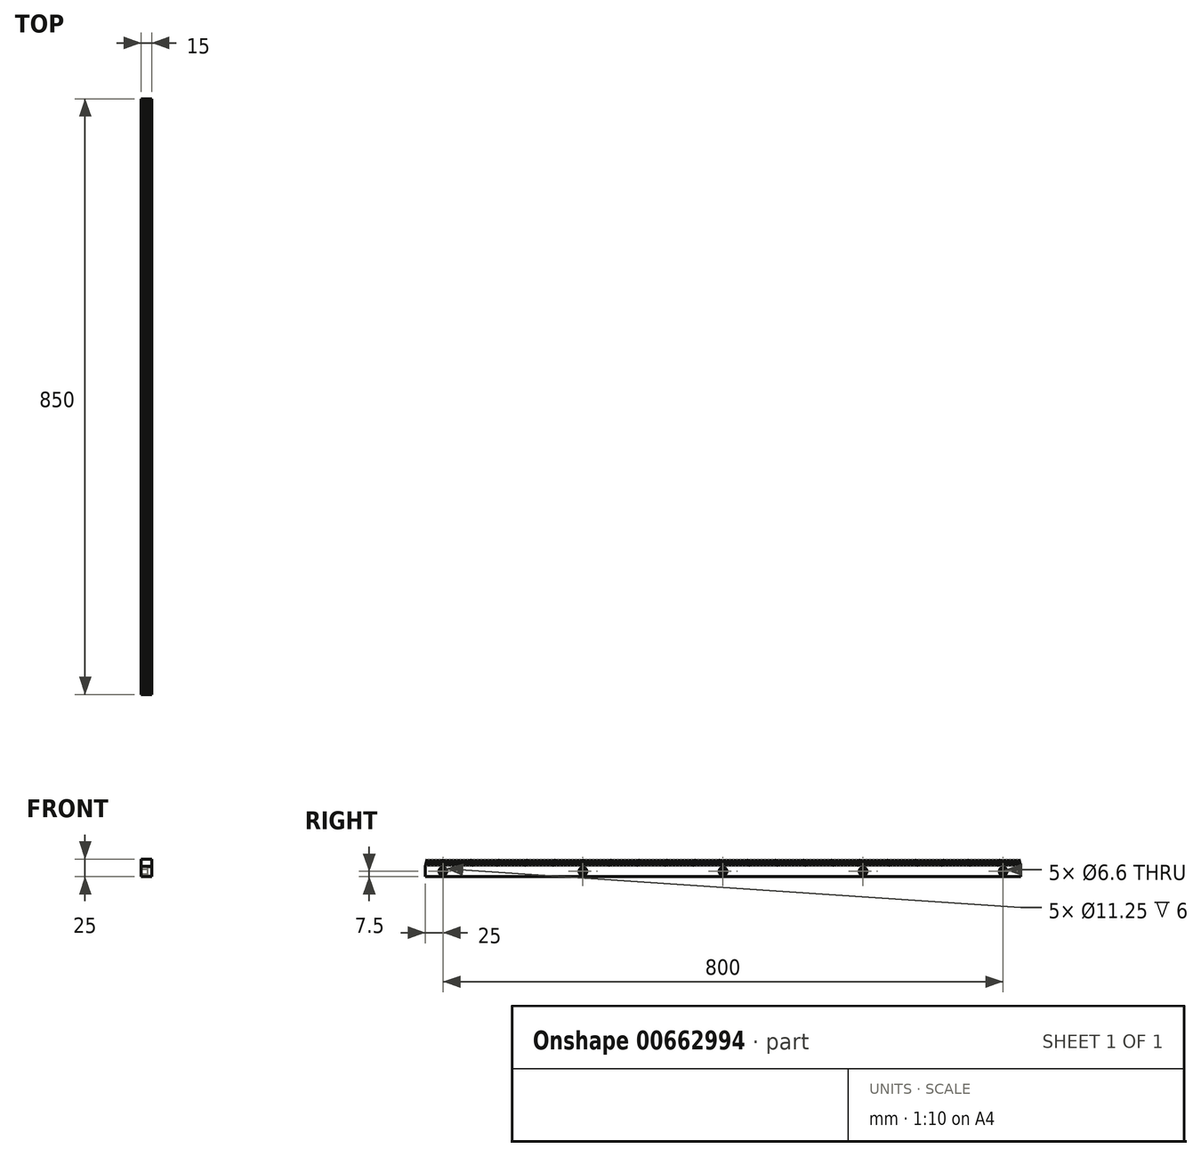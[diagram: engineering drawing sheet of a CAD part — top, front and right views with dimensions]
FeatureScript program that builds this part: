
annotation { "Feature Type Name" : "Feature", "Feature Type Description" : "" }
export const myFeature = defineFeature(function(context is Context, id is Id, definition is map)
    precondition{}
    {
        {
            var Q0;
            Q0=qCreatedBy(makeId("Right.planeOp"),FACE);
            var sketch = newSketch(context, id + "F0", { "sketchPlane" : qUnion([Q0])});
            skLineSegment(sketch, "E0", {"start": v(0, 0) * mm, "end": v(2.5, 10) * mm});
            skLineSegment(sketch, "E1", {"start": v(2.5, 10) * mm, "end": v(5, 0) * mm});
            skLineSegment(sketch, "E2.1.0.0", {"start": v(5, 0) * mm, "end": v(7.5, 10) * mm});
            skLineSegment(sketch, "E2.1.0.1", {"start": v(7.5, 10) * mm, "end": v(10, 0) * mm});
            skLineSegment(sketch, "E2.2.0.0", {"start": v(10, 0) * mm, "end": v(12.5, 10) * mm});
            skLineSegment(sketch, "E2.2.0.1", {"start": v(12.5, 10) * mm, "end": v(15, 0) * mm});
            skLineSegment(sketch, "E2.3.0.0", {"start": v(15, 0) * mm, "end": v(17.5, 10) * mm});
            skLineSegment(sketch, "E2.3.0.1", {"start": v(17.5, 10) * mm, "end": v(20, 0) * mm});
            skLineSegment(sketch, "E2.4.0.0", {"start": v(20, 0) * mm, "end": v(22.5, 10) * mm});
            skLineSegment(sketch, "E2.4.0.1", {"start": v(22.5, 10) * mm, "end": v(25, 0) * mm});
            skLineSegment(sketch, "E2.5.0.0", {"start": v(25, 0) * mm, "end": v(27.5, 10) * mm});
            skLineSegment(sketch, "E2.5.0.1", {"start": v(27.5, 10) * mm, "end": v(30, 0) * mm});
            skLineSegment(sketch, "E2.6.0.0", {"start": v(30, 0) * mm, "end": v(32.5, 10) * mm});
            skLineSegment(sketch, "E2.6.0.1", {"start": v(32.5, 10) * mm, "end": v(35, 0) * mm});
            skLineSegment(sketch, "E2.7.0.0", {"start": v(35, 0) * mm, "end": v(37.5, 10) * mm});
            skLineSegment(sketch, "E2.7.0.1", {"start": v(37.5, 10) * mm, "end": v(40, 0) * mm});
            skLineSegment(sketch, "E2.8.0.0", {"start": v(40, 0) * mm, "end": v(42.5, 10) * mm});
            skLineSegment(sketch, "E2.8.0.1", {"start": v(42.5, 10) * mm, "end": v(45, 0) * mm});
            skLineSegment(sketch, "E2.9.0.0", {"start": v(45, 0) * mm, "end": v(47.5, 10) * mm});
            skLineSegment(sketch, "E2.9.0.1", {"start": v(47.5, 10) * mm, "end": v(50, 0) * mm});
            skLineSegment(sketch, "E2.10.0.0", {"start": v(50, 0) * mm, "end": v(52.5, 10) * mm});
            skLineSegment(sketch, "E2.10.0.1", {"start": v(52.5, 10) * mm, "end": v(55, 0) * mm});
            skLineSegment(sketch, "E2.11.0.0", {"start": v(55, 0) * mm, "end": v(57.5, 10) * mm});
            skLineSegment(sketch, "E2.11.0.1", {"start": v(57.5, 10) * mm, "end": v(60, 0) * mm});
            skLineSegment(sketch, "E2.12.0.0", {"start": v(60, 0) * mm, "end": v(62.5, 10) * mm});
            skLineSegment(sketch, "E2.12.0.1", {"start": v(62.5, 10) * mm, "end": v(65, 0) * mm});
            skLineSegment(sketch, "E2.13.0.0", {"start": v(65, 0) * mm, "end": v(67.5, 10) * mm});
            skLineSegment(sketch, "E2.13.0.1", {"start": v(67.5, 10) * mm, "end": v(70, 0) * mm});
            skLineSegment(sketch, "E2.14.0.0", {"start": v(70, 0) * mm, "end": v(72.5, 10) * mm});
            skLineSegment(sketch, "E2.14.0.1", {"start": v(72.5, 10) * mm, "end": v(75, 0) * mm});
            skLineSegment(sketch, "E2.15.0.0", {"start": v(75, 0) * mm, "end": v(77.5, 10) * mm});
            skLineSegment(sketch, "E2.15.0.1", {"start": v(77.5, 10) * mm, "end": v(80, 0) * mm});
            skLineSegment(sketch, "E2.16.0.0", {"start": v(80, 0) * mm, "end": v(82.5, 10) * mm});
            skLineSegment(sketch, "E2.16.0.1", {"start": v(82.5, 10) * mm, "end": v(85, 0) * mm});
            skLineSegment(sketch, "E2.17.0.0", {"start": v(85, 0) * mm, "end": v(87.5, 10) * mm});
            skLineSegment(sketch, "E2.17.0.1", {"start": v(87.5, 10) * mm, "end": v(90, 0) * mm});
            skLineSegment(sketch, "E2.18.0.0", {"start": v(90, 0) * mm, "end": v(92.5, 10) * mm});
            skLineSegment(sketch, "E2.18.0.1", {"start": v(92.5, 10) * mm, "end": v(95, 0) * mm});
            skLineSegment(sketch, "E2.19.0.0", {"start": v(95, 0) * mm, "end": v(97.5, 10) * mm});
            skLineSegment(sketch, "E2.19.0.1", {"start": v(97.5, 10) * mm, "end": v(100, 0) * mm});
            skLineSegment(sketch, "E2.20.0.0", {"start": v(100, 0) * mm, "end": v(102.5, 10) * mm});
            skLineSegment(sketch, "E2.20.0.1", {"start": v(102.5, 10) * mm, "end": v(105, 0) * mm});
            skLineSegment(sketch, "E2.21.0.0", {"start": v(105, 0) * mm, "end": v(107.5, 10) * mm});
            skLineSegment(sketch, "E2.21.0.1", {"start": v(107.5, 10) * mm, "end": v(110, 0) * mm});
            skLineSegment(sketch, "E2.22.0.0", {"start": v(110, 0) * mm, "end": v(112.5, 10) * mm});
            skLineSegment(sketch, "E2.22.0.1", {"start": v(112.5, 10) * mm, "end": v(115, 0) * mm});
            skLineSegment(sketch, "E2.23.0.0", {"start": v(115, 0) * mm, "end": v(117.5, 10) * mm});
            skLineSegment(sketch, "E2.23.0.1", {"start": v(117.5, 10) * mm, "end": v(120, 0) * mm});
            skLineSegment(sketch, "E2.24.0.0", {"start": v(120, 0) * mm, "end": v(122.5, 10) * mm});
            skLineSegment(sketch, "E2.24.0.1", {"start": v(122.5, 10) * mm, "end": v(125, 0) * mm});
            skLineSegment(sketch, "E2.25.0.0", {"start": v(125, 0) * mm, "end": v(127.5, 10) * mm});
            skLineSegment(sketch, "E2.25.0.1", {"start": v(127.5, 10) * mm, "end": v(130, 0) * mm});
            skLineSegment(sketch, "E2.26.0.0", {"start": v(130, 0) * mm, "end": v(132.5, 10) * mm});
            skLineSegment(sketch, "E2.26.0.1", {"start": v(132.5, 10) * mm, "end": v(135, 0) * mm});
            skLineSegment(sketch, "E2.27.0.0", {"start": v(135, 0) * mm, "end": v(137.5, 10) * mm});
            skLineSegment(sketch, "E2.27.0.1", {"start": v(137.5, 10) * mm, "end": v(140, 0) * mm});
            skLineSegment(sketch, "E2.28.0.0", {"start": v(140, 0) * mm, "end": v(142.5, 10) * mm});
            skLineSegment(sketch, "E2.28.0.1", {"start": v(142.5, 10) * mm, "end": v(145, 0) * mm});
            skLineSegment(sketch, "E2.29.0.0", {"start": v(145, 0) * mm, "end": v(147.5, 10) * mm});
            skLineSegment(sketch, "E2.29.0.1", {"start": v(147.5, 10) * mm, "end": v(150, 0) * mm});
            skLineSegment(sketch, "E2.30.0.0", {"start": v(150, 0) * mm, "end": v(152.5, 10) * mm});
            skLineSegment(sketch, "E2.30.0.1", {"start": v(152.5, 10) * mm, "end": v(155, 0) * mm});
            skLineSegment(sketch, "E2.31.0.0", {"start": v(155, 0) * mm, "end": v(157.5, 10) * mm});
            skLineSegment(sketch, "E2.31.0.1", {"start": v(157.5, 10) * mm, "end": v(160, 0) * mm});
            skLineSegment(sketch, "E2.32.0.0", {"start": v(160, 0) * mm, "end": v(162.5, 10) * mm});
            skLineSegment(sketch, "E2.32.0.1", {"start": v(162.5, 10) * mm, "end": v(165, 0) * mm});
            skLineSegment(sketch, "E2.33.0.0", {"start": v(165, 0) * mm, "end": v(167.5, 10) * mm});
            skLineSegment(sketch, "E2.33.0.1", {"start": v(167.5, 10) * mm, "end": v(170, 0) * mm});
            skLineSegment(sketch, "E2.34.0.0", {"start": v(170, 0) * mm, "end": v(172.5, 10) * mm});
            skLineSegment(sketch, "E2.34.0.1", {"start": v(172.5, 10) * mm, "end": v(175, 0) * mm});
            skLineSegment(sketch, "E2.35.0.0", {"start": v(175, 0) * mm, "end": v(177.5, 10) * mm});
            skLineSegment(sketch, "E2.35.0.1", {"start": v(177.5, 10) * mm, "end": v(180, 0) * mm});
            skLineSegment(sketch, "E2.36.0.0", {"start": v(180, 0) * mm, "end": v(182.5, 10) * mm});
            skLineSegment(sketch, "E2.36.0.1", {"start": v(182.5, 10) * mm, "end": v(185, 0) * mm});
            skLineSegment(sketch, "E2.37.0.0", {"start": v(185, 0) * mm, "end": v(187.5, 10) * mm});
            skLineSegment(sketch, "E2.37.0.1", {"start": v(187.5, 10) * mm, "end": v(190, 0) * mm});
            skLineSegment(sketch, "E2.38.0.0", {"start": v(190, 0) * mm, "end": v(192.5, 10) * mm});
            skLineSegment(sketch, "E2.38.0.1", {"start": v(192.5, 10) * mm, "end": v(195, 0) * mm});
            skLineSegment(sketch, "E2.39.0.0", {"start": v(195, 0) * mm, "end": v(197.5, 10) * mm});
            skLineSegment(sketch, "E2.39.0.1", {"start": v(197.5, 10) * mm, "end": v(200, 0) * mm});
            skLineSegment(sketch, "E2.40.0.0", {"start": v(200, 0) * mm, "end": v(202.5, 10) * mm});
            skLineSegment(sketch, "E2.40.0.1", {"start": v(202.5, 10) * mm, "end": v(205, 0) * mm});
            skLineSegment(sketch, "E2.41.0.0", {"start": v(205, 0) * mm, "end": v(207.5, 10) * mm});
            skLineSegment(sketch, "E2.41.0.1", {"start": v(207.5, 10) * mm, "end": v(210, 0) * mm});
            skLineSegment(sketch, "E2.42.0.0", {"start": v(210, 0) * mm, "end": v(212.5, 10) * mm});
            skLineSegment(sketch, "E2.42.0.1", {"start": v(212.5, 10) * mm, "end": v(215, 0) * mm});
            skLineSegment(sketch, "E2.43.0.0", {"start": v(215, 0) * mm, "end": v(217.5, 10) * mm});
            skLineSegment(sketch, "E2.43.0.1", {"start": v(217.5, 10) * mm, "end": v(220, 0) * mm});
            skLineSegment(sketch, "E2.44.0.0", {"start": v(220, 0) * mm, "end": v(222.5, 10) * mm});
            skLineSegment(sketch, "E2.44.0.1", {"start": v(222.5, 10) * mm, "end": v(225, 0) * mm});
            skLineSegment(sketch, "E2.45.0.0", {"start": v(225, 0) * mm, "end": v(227.5, 10) * mm});
            skLineSegment(sketch, "E2.45.0.1", {"start": v(227.5, 10) * mm, "end": v(230, 0) * mm});
            skLineSegment(sketch, "E2.46.0.0", {"start": v(230, 0) * mm, "end": v(232.5, 10) * mm});
            skLineSegment(sketch, "E2.46.0.1", {"start": v(232.5, 10) * mm, "end": v(235, 0) * mm});
            skLineSegment(sketch, "E2.47.0.0", {"start": v(235, 0) * mm, "end": v(237.5, 10) * mm});
            skLineSegment(sketch, "E2.47.0.1", {"start": v(237.5, 10) * mm, "end": v(240, 0) * mm});
            skLineSegment(sketch, "E2.48.0.0", {"start": v(240, 0) * mm, "end": v(242.5, 10) * mm});
            skLineSegment(sketch, "E2.48.0.1", {"start": v(242.5, 10) * mm, "end": v(245, 0) * mm});
            skLineSegment(sketch, "E2.49.0.0", {"start": v(245, 0) * mm, "end": v(247.5, 10) * mm});
            skLineSegment(sketch, "E2.49.0.1", {"start": v(247.5, 10) * mm, "end": v(250, 0) * mm});
            skLineSegment(sketch, "E2.50.0.0", {"start": v(250, 0) * mm, "end": v(252.5, 10) * mm});
            skLineSegment(sketch, "E2.50.0.1", {"start": v(252.5, 10) * mm, "end": v(255, 0) * mm});
            skLineSegment(sketch, "E2.51.0.0", {"start": v(255, 0) * mm, "end": v(257.5, 10) * mm});
            skLineSegment(sketch, "E2.51.0.1", {"start": v(257.5, 10) * mm, "end": v(260, 0) * mm});
            skLineSegment(sketch, "E2.52.0.0", {"start": v(260, 0) * mm, "end": v(262.5, 10) * mm});
            skLineSegment(sketch, "E2.52.0.1", {"start": v(262.5, 10) * mm, "end": v(265, 0) * mm});
            skLineSegment(sketch, "E2.53.0.0", {"start": v(265, 0) * mm, "end": v(267.5, 10) * mm});
            skLineSegment(sketch, "E2.53.0.1", {"start": v(267.5, 10) * mm, "end": v(270, 0) * mm});
            skLineSegment(sketch, "E2.54.0.0", {"start": v(270, 0) * mm, "end": v(272.5, 10) * mm});
            skLineSegment(sketch, "E2.54.0.1", {"start": v(272.5, 10) * mm, "end": v(275, 0) * mm});
            skLineSegment(sketch, "E2.55.0.0", {"start": v(275, 0) * mm, "end": v(277.5, 10) * mm});
            skLineSegment(sketch, "E2.55.0.1", {"start": v(277.5, 10) * mm, "end": v(280, 0) * mm});
            skLineSegment(sketch, "E2.56.0.0", {"start": v(280, 0) * mm, "end": v(282.5, 10) * mm});
            skLineSegment(sketch, "E2.56.0.1", {"start": v(282.5, 10) * mm, "end": v(285, 0) * mm});
            skLineSegment(sketch, "E2.57.0.0", {"start": v(285, 0) * mm, "end": v(287.5, 10) * mm});
            skLineSegment(sketch, "E2.57.0.1", {"start": v(287.5, 10) * mm, "end": v(290, 0) * mm});
            skLineSegment(sketch, "E2.58.0.0", {"start": v(290, 0) * mm, "end": v(292.5, 10) * mm});
            skLineSegment(sketch, "E2.58.0.1", {"start": v(292.5, 10) * mm, "end": v(295, 0) * mm});
            skLineSegment(sketch, "E2.59.0.0", {"start": v(295, 0) * mm, "end": v(297.5, 10) * mm});
            skLineSegment(sketch, "E2.59.0.1", {"start": v(297.5, 10) * mm, "end": v(300, 0) * mm});
            skLineSegment(sketch, "E2.60.0.0", {"start": v(300, 0) * mm, "end": v(302.5, 10) * mm});
            skLineSegment(sketch, "E2.60.0.1", {"start": v(302.5, 10) * mm, "end": v(305, 0) * mm});
            skLineSegment(sketch, "E2.61.0.0", {"start": v(305, 0) * mm, "end": v(307.5, 10) * mm});
            skLineSegment(sketch, "E2.61.0.1", {"start": v(307.5, 10) * mm, "end": v(310, 0) * mm});
            skLineSegment(sketch, "E2.62.0.0", {"start": v(310, 0) * mm, "end": v(312.5, 10) * mm});
            skLineSegment(sketch, "E2.62.0.1", {"start": v(312.5, 10) * mm, "end": v(315, 0) * mm});
            skLineSegment(sketch, "E2.63.0.0", {"start": v(315, 0) * mm, "end": v(317.5, 10) * mm});
            skLineSegment(sketch, "E2.63.0.1", {"start": v(317.5, 10) * mm, "end": v(320, 0) * mm});
            skLineSegment(sketch, "E2.64.0.0", {"start": v(320, 0) * mm, "end": v(322.5, 10) * mm});
            skLineSegment(sketch, "E2.64.0.1", {"start": v(322.5, 10) * mm, "end": v(325, 0) * mm});
            skLineSegment(sketch, "E2.65.0.0", {"start": v(325, 0) * mm, "end": v(327.5, 10) * mm});
            skLineSegment(sketch, "E2.65.0.1", {"start": v(327.5, 10) * mm, "end": v(330, 0) * mm});
            skLineSegment(sketch, "E2.66.0.0", {"start": v(330, 0) * mm, "end": v(332.5, 10) * mm});
            skLineSegment(sketch, "E2.66.0.1", {"start": v(332.5, 10) * mm, "end": v(335, 0) * mm});
            skLineSegment(sketch, "E2.67.0.0", {"start": v(335, 0) * mm, "end": v(337.5, 10) * mm});
            skLineSegment(sketch, "E2.67.0.1", {"start": v(337.5, 10) * mm, "end": v(340, 0) * mm});
            skLineSegment(sketch, "E2.68.0.0", {"start": v(340, 0) * mm, "end": v(342.5, 10) * mm});
            skLineSegment(sketch, "E2.68.0.1", {"start": v(342.5, 10) * mm, "end": v(345, 0) * mm});
            skLineSegment(sketch, "E2.69.0.0", {"start": v(345, 0) * mm, "end": v(347.5, 10) * mm});
            skLineSegment(sketch, "E2.69.0.1", {"start": v(347.5, 10) * mm, "end": v(350, 0) * mm});
            skLineSegment(sketch, "E2.70.0.0", {"start": v(350, 0) * mm, "end": v(352.5, 10) * mm});
            skLineSegment(sketch, "E2.70.0.1", {"start": v(352.5, 10) * mm, "end": v(355, 0) * mm});
            skLineSegment(sketch, "E2.71.0.0", {"start": v(355, 0) * mm, "end": v(357.5, 10) * mm});
            skLineSegment(sketch, "E2.71.0.1", {"start": v(357.5, 10) * mm, "end": v(360, 0) * mm});
            skLineSegment(sketch, "E2.72.0.0", {"start": v(360, 0) * mm, "end": v(362.5, 10) * mm});
            skLineSegment(sketch, "E2.72.0.1", {"start": v(362.5, 10) * mm, "end": v(365, 0) * mm});
            skLineSegment(sketch, "E2.73.0.0", {"start": v(365, 0) * mm, "end": v(367.5, 10) * mm});
            skLineSegment(sketch, "E2.73.0.1", {"start": v(367.5, 10) * mm, "end": v(370, 0) * mm});
            skLineSegment(sketch, "E2.74.0.0", {"start": v(370, 0) * mm, "end": v(372.5, 10) * mm});
            skLineSegment(sketch, "E2.74.0.1", {"start": v(372.5, 10) * mm, "end": v(375, 0) * mm});
            skLineSegment(sketch, "E2.75.0.0", {"start": v(375, 0) * mm, "end": v(377.5, 10) * mm});
            skLineSegment(sketch, "E2.75.0.1", {"start": v(377.5, 10) * mm, "end": v(380, 0) * mm});
            skLineSegment(sketch, "E2.76.0.0", {"start": v(380, 0) * mm, "end": v(382.5, 10) * mm});
            skLineSegment(sketch, "E2.76.0.1", {"start": v(382.5, 10) * mm, "end": v(385, 0) * mm});
            skLineSegment(sketch, "E2.77.0.0", {"start": v(385, 0) * mm, "end": v(387.5, 10) * mm});
            skLineSegment(sketch, "E2.77.0.1", {"start": v(387.5, 10) * mm, "end": v(390, 0) * mm});
            skLineSegment(sketch, "E2.78.0.0", {"start": v(390, 0) * mm, "end": v(392.5, 10) * mm});
            skLineSegment(sketch, "E2.78.0.1", {"start": v(392.5, 10) * mm, "end": v(395, 0) * mm});
            skLineSegment(sketch, "E2.79.0.0", {"start": v(395, 0) * mm, "end": v(397.5, 10) * mm});
            skLineSegment(sketch, "E2.79.0.1", {"start": v(397.5, 10) * mm, "end": v(400, 0) * mm});
            skLineSegment(sketch, "E2.80.0.0", {"start": v(400, 0) * mm, "end": v(402.5, 10) * mm});
            skLineSegment(sketch, "E2.80.0.1", {"start": v(402.5, 10) * mm, "end": v(405, 0) * mm});
            skLineSegment(sketch, "E2.81.0.0", {"start": v(405, 0) * mm, "end": v(407.5, 10) * mm});
            skLineSegment(sketch, "E2.81.0.1", {"start": v(407.5, 10) * mm, "end": v(410, 0) * mm});
            skLineSegment(sketch, "E2.82.0.0", {"start": v(410, 0) * mm, "end": v(412.5, 10) * mm});
            skLineSegment(sketch, "E2.82.0.1", {"start": v(412.5, 10) * mm, "end": v(415, 0) * mm});
            skLineSegment(sketch, "E2.83.0.0", {"start": v(415, 0) * mm, "end": v(417.5, 10) * mm});
            skLineSegment(sketch, "E2.83.0.1", {"start": v(417.5, 10) * mm, "end": v(420, 0) * mm});
            skLineSegment(sketch, "E2.84.0.0", {"start": v(420, 0) * mm, "end": v(422.5, 10) * mm});
            skLineSegment(sketch, "E2.84.0.1", {"start": v(422.5, 10) * mm, "end": v(425, 0) * mm});
            skLineSegment(sketch, "E2.direction1", {"start": v(0, 0) * mm, "end": v(5, 0) * mm, "construction": true});
            skLineSegment(sketch, "E3.1.0.0", {"start": v(847.5, 10) * mm, "end": v(850, 0) * mm});
            skLineSegment(sketch, "E3.1.0.1", {"start": v(427.5, 10) * mm, "end": v(430, 0) * mm});
            skLineSegment(sketch, "E3.1.0.2", {"start": v(432.5, 10) * mm, "end": v(435, 0) * mm});
            skLineSegment(sketch, "E3.1.0.3", {"start": v(437.5, 10) * mm, "end": v(440, 0) * mm});
            skLineSegment(sketch, "E3.1.0.4", {"start": v(845, 0) * mm, "end": v(847.5, 10) * mm});
            skLineSegment(sketch, "E3.1.0.5", {"start": v(442.5, 10) * mm, "end": v(445, 0) * mm});
            skLineSegment(sketch, "E3.1.0.6", {"start": v(447.5, 10) * mm, "end": v(450, 0) * mm});
            skLineSegment(sketch, "E3.1.0.7", {"start": v(450, 0) * mm, "end": v(452.5, 10) * mm});
            skLineSegment(sketch, "E3.1.0.8", {"start": v(587.5, 10) * mm, "end": v(590, 0) * mm});
            skLineSegment(sketch, "E3.1.0.9", {"start": v(590, 0) * mm, "end": v(592.5, 10) * mm});
            skLineSegment(sketch, "E3.1.0.10", {"start": v(585, 0) * mm, "end": v(587.5, 10) * mm});
            skLineSegment(sketch, "E3.1.0.11", {"start": v(842.5, 10) * mm, "end": v(845, 0) * mm});
            skLineSegment(sketch, "E3.1.0.12", {"start": v(462.5, 10) * mm, "end": v(465, 0) * mm});
            skLineSegment(sketch, "E3.1.0.13", {"start": v(460, 0) * mm, "end": v(462.5, 10) * mm});
            skLineSegment(sketch, "E3.1.0.14", {"start": v(425, 0) * mm, "end": v(427.5, 10) * mm});
            skLineSegment(sketch, "E3.1.0.15", {"start": v(430, 0) * mm, "end": v(432.5, 10) * mm});
            skLineSegment(sketch, "E3.1.0.16", {"start": v(435, 0) * mm, "end": v(437.5, 10) * mm});
            skLineSegment(sketch, "E3.1.0.17", {"start": v(557.5, 10) * mm, "end": v(560, 0) * mm});
            skLineSegment(sketch, "E3.1.0.18", {"start": v(517.5, 10) * mm, "end": v(520, 0) * mm});
            skLineSegment(sketch, "E3.1.0.19", {"start": v(477.5, 10) * mm, "end": v(480, 0) * mm});
            skLineSegment(sketch, "E3.1.0.20", {"start": v(440, 0) * mm, "end": v(442.5, 10) * mm});
            skLineSegment(sketch, "E3.1.0.21", {"start": v(677.5, 10) * mm, "end": v(680, 0) * mm});
            skLineSegment(sketch, "E3.1.0.22", {"start": v(637.5, 10) * mm, "end": v(640, 0) * mm});
            skLineSegment(sketch, "E3.1.0.23", {"start": v(597.5, 10) * mm, "end": v(600, 0) * mm});
            skLineSegment(sketch, "E3.1.0.24", {"start": v(542.5, 10) * mm, "end": v(545, 0) * mm});
            skLineSegment(sketch, "E3.1.0.25", {"start": v(552.5, 10) * mm, "end": v(555, 0) * mm});
            skLineSegment(sketch, "E3.1.0.26", {"start": v(512.5, 10) * mm, "end": v(515, 0) * mm});
            skLineSegment(sketch, "E3.1.0.27", {"start": v(502.5, 10) * mm, "end": v(505, 0) * mm});
            skLineSegment(sketch, "E3.1.0.28", {"start": v(837.5, 10) * mm, "end": v(840, 0) * mm});
            skLineSegment(sketch, "E3.1.0.29", {"start": v(472.5, 10) * mm, "end": v(475, 0) * mm});
            skLineSegment(sketch, "E3.1.0.30", {"start": v(797.5, 10) * mm, "end": v(800, 0) * mm});
            skLineSegment(sketch, "E3.1.0.31", {"start": v(445, 0) * mm, "end": v(447.5, 10) * mm});
            skLineSegment(sketch, "E3.1.0.32", {"start": v(702.5, 10) * mm, "end": v(705, 0) * mm});
            skLineSegment(sketch, "E3.1.0.33", {"start": v(712.5, 10) * mm, "end": v(715, 0) * mm});
            skLineSegment(sketch, "E3.1.0.34", {"start": v(662.5, 10) * mm, "end": v(665, 0) * mm});
            skLineSegment(sketch, "E3.1.0.35", {"start": v(672.5, 10) * mm, "end": v(675, 0) * mm});
            skLineSegment(sketch, "E3.1.0.36", {"start": v(622.5, 10) * mm, "end": v(625, 0) * mm});
            skLineSegment(sketch, "E3.1.0.37", {"start": v(632.5, 10) * mm, "end": v(635, 0) * mm});
            skLineSegment(sketch, "E3.1.0.38", {"start": v(592.5, 10) * mm, "end": v(595, 0) * mm});
            skLineSegment(sketch, "E3.1.0.39", {"start": v(582.5, 10) * mm, "end": v(585, 0) * mm});
            skLineSegment(sketch, "E3.1.0.40", {"start": v(547.5, 10) * mm, "end": v(550, 0) * mm});
            skLineSegment(sketch, "E3.1.0.41", {"start": v(507.5, 10) * mm, "end": v(510, 0) * mm});
            skLineSegment(sketch, "E3.1.0.42", {"start": v(832.5, 10) * mm, "end": v(835, 0) * mm});
            skLineSegment(sketch, "E3.1.0.43", {"start": v(467.5, 10) * mm, "end": v(470, 0) * mm});
            skLineSegment(sketch, "E3.1.0.44", {"start": v(792.5, 10) * mm, "end": v(795, 0) * mm});
            skLineSegment(sketch, "E3.1.0.45", {"start": v(752.5, 10) * mm, "end": v(755, 0) * mm});
            skLineSegment(sketch, "E3.1.0.46", {"start": v(707.5, 10) * mm, "end": v(710, 0) * mm});
            skLineSegment(sketch, "E3.1.0.47", {"start": v(667.5, 10) * mm, "end": v(670, 0) * mm});
            skLineSegment(sketch, "E3.1.0.48", {"start": v(627.5, 10) * mm, "end": v(630, 0) * mm});
            skLineSegment(sketch, "E3.1.0.49", {"start": v(452.5, 10) * mm, "end": v(455, 0) * mm});
            skLineSegment(sketch, "E3.1.0.50", {"start": v(455, 0) * mm, "end": v(457.5, 10) * mm});
            skLineSegment(sketch, "E3.1.0.51", {"start": v(800, 0) * mm, "end": v(802.5, 10) * mm});
            skLineSegment(sketch, "E3.1.0.52", {"start": v(760, 0) * mm, "end": v(762.5, 10) * mm});
            skLineSegment(sketch, "E3.1.0.53", {"start": v(720, 0) * mm, "end": v(722.5, 10) * mm});
            skLineSegment(sketch, "E3.1.0.54", {"start": v(680, 0) * mm, "end": v(682.5, 10) * mm});
            skLineSegment(sketch, "E3.1.0.55", {"start": v(840, 0) * mm, "end": v(842.5, 10) * mm});
            skLineSegment(sketch, "E3.1.0.56", {"start": v(802.5, 10) * mm, "end": v(805, 0) * mm});
            skLineSegment(sketch, "E3.1.0.57", {"start": v(722.5, 10) * mm, "end": v(725, 0) * mm});
            skLineSegment(sketch, "E3.1.0.58", {"start": v(682.5, 10) * mm, "end": v(685, 0) * mm});
            skLineSegment(sketch, "E3.1.0.59", {"start": v(555, 0) * mm, "end": v(557.5, 10) * mm});
            skLineSegment(sketch, "E3.1.0.60", {"start": v(515, 0) * mm, "end": v(517.5, 10) * mm});
            skLineSegment(sketch, "E3.1.0.61", {"start": v(475, 0) * mm, "end": v(477.5, 10) * mm});
            skLineSegment(sketch, "E3.1.0.62", {"start": v(715, 0) * mm, "end": v(717.5, 10) * mm});
            skLineSegment(sketch, "E3.1.0.63", {"start": v(675, 0) * mm, "end": v(677.5, 10) * mm});
            skLineSegment(sketch, "E3.1.0.64", {"start": v(635, 0) * mm, "end": v(637.5, 10) * mm});
            skLineSegment(sketch, "E3.1.0.65", {"start": v(595, 0) * mm, "end": v(597.5, 10) * mm});
            skLineSegment(sketch, "E3.1.0.66", {"start": v(550, 0) * mm, "end": v(552.5, 10) * mm});
            skLineSegment(sketch, "E3.1.0.67", {"start": v(510, 0) * mm, "end": v(512.5, 10) * mm});
            skLineSegment(sketch, "E3.1.0.68", {"start": v(835, 0) * mm, "end": v(837.5, 10) * mm});
            skLineSegment(sketch, "E3.1.0.69", {"start": v(470, 0) * mm, "end": v(472.5, 10) * mm});
            skLineSegment(sketch, "E3.1.0.70", {"start": v(795, 0) * mm, "end": v(797.5, 10) * mm});
            skLineSegment(sketch, "E3.1.0.71", {"start": v(755, 0) * mm, "end": v(757.5, 10) * mm});
            skLineSegment(sketch, "E3.1.0.72", {"start": v(710, 0) * mm, "end": v(712.5, 10) * mm});
            skLineSegment(sketch, "E3.1.0.73", {"start": v(670, 0) * mm, "end": v(672.5, 10) * mm});
            skLineSegment(sketch, "E3.1.0.74", {"start": v(630, 0) * mm, "end": v(632.5, 10) * mm});
            skLineSegment(sketch, "E3.1.0.75", {"start": v(545, 0) * mm, "end": v(547.5, 10) * mm});
            skLineSegment(sketch, "E3.1.0.76", {"start": v(505, 0) * mm, "end": v(507.5, 10) * mm});
            skLineSegment(sketch, "E3.1.0.77", {"start": v(830, 0) * mm, "end": v(832.5, 10) * mm});
            skLineSegment(sketch, "E3.1.0.78", {"start": v(465, 0) * mm, "end": v(467.5, 10) * mm});
            skLineSegment(sketch, "E3.1.0.79", {"start": v(790, 0) * mm, "end": v(792.5, 10) * mm});
            skLineSegment(sketch, "E3.1.0.80", {"start": v(750, 0) * mm, "end": v(752.5, 10) * mm});
            skLineSegment(sketch, "E3.1.0.81", {"start": v(705, 0) * mm, "end": v(707.5, 10) * mm});
            skLineSegment(sketch, "E3.1.0.82", {"start": v(665, 0) * mm, "end": v(667.5, 10) * mm});
            skLineSegment(sketch, "E3.1.0.83", {"start": v(625, 0) * mm, "end": v(627.5, 10) * mm});
            skLineSegment(sketch, "E3.1.0.84", {"start": v(457.5, 10) * mm, "end": v(460, 0) * mm});
            skLineSegment(sketch, "E3.1.0.85", {"start": v(495, 0) * mm, "end": v(497.5, 10) * mm});
            skLineSegment(sketch, "E3.1.0.86", {"start": v(655, 0) * mm, "end": v(657.5, 10) * mm});
            skLineSegment(sketch, "E3.1.0.87", {"start": v(615, 0) * mm, "end": v(617.5, 10) * mm});
            skLineSegment(sketch, "E3.1.0.88", {"start": v(575, 0) * mm, "end": v(577.5, 10) * mm});
            skLineSegment(sketch, "E3.1.0.89", {"start": v(535, 0) * mm, "end": v(537.5, 10) * mm});
            skLineSegment(sketch, "E3.1.0.90", {"start": v(490, 0) * mm, "end": v(492.5, 10) * mm});
            skLineSegment(sketch, "E3.1.0.91", {"start": v(815, 0) * mm, "end": v(817.5, 10) * mm});
            skLineSegment(sketch, "E3.1.0.92", {"start": v(775, 0) * mm, "end": v(777.5, 10) * mm});
            skLineSegment(sketch, "E3.1.0.93", {"start": v(735, 0) * mm, "end": v(737.5, 10) * mm});
            skLineSegment(sketch, "E3.1.0.94", {"start": v(695, 0) * mm, "end": v(697.5, 10) * mm});
            skLineSegment(sketch, "E3.1.0.95", {"start": v(650, 0) * mm, "end": v(652.5, 10) * mm});
            skLineSegment(sketch, "E3.1.0.96", {"start": v(610, 0) * mm, "end": v(612.5, 10) * mm});
            skLineSegment(sketch, "E3.1.0.97", {"start": v(570, 0) * mm, "end": v(572.5, 10) * mm});
            skLineSegment(sketch, "E3.1.0.98", {"start": v(530, 0) * mm, "end": v(532.5, 10) * mm});
            skLineSegment(sketch, "E3.1.0.99", {"start": v(485, 0) * mm, "end": v(487.5, 10) * mm});
            skLineSegment(sketch, "E3.1.0.100", {"start": v(810, 0) * mm, "end": v(812.5, 10) * mm});
            skLineSegment(sketch, "E3.1.0.101", {"start": v(770, 0) * mm, "end": v(772.5, 10) * mm});
            skLineSegment(sketch, "E3.1.0.102", {"start": v(730, 0) * mm, "end": v(732.5, 10) * mm});
            skLineSegment(sketch, "E3.1.0.103", {"start": v(690, 0) * mm, "end": v(692.5, 10) * mm});
            skLineSegment(sketch, "E3.1.0.104", {"start": v(645, 0) * mm, "end": v(647.5, 10) * mm});
            skLineSegment(sketch, "E3.1.0.105", {"start": v(605, 0) * mm, "end": v(607.5, 10) * mm});
            skLineSegment(sketch, "E3.1.0.106", {"start": v(565, 0) * mm, "end": v(567.5, 10) * mm});
            skLineSegment(sketch, "E3.1.0.107", {"start": v(525, 0) * mm, "end": v(527.5, 10) * mm});
            skLineSegment(sketch, "E3.1.0.108", {"start": v(480, 0) * mm, "end": v(482.5, 10) * mm});
            skLineSegment(sketch, "E3.1.0.109", {"start": v(805, 0) * mm, "end": v(807.5, 10) * mm});
            skLineSegment(sketch, "E3.1.0.110", {"start": v(765, 0) * mm, "end": v(767.5, 10) * mm});
            skLineSegment(sketch, "E3.1.0.111", {"start": v(725, 0) * mm, "end": v(727.5, 10) * mm});
            skLineSegment(sketch, "E3.1.0.112", {"start": v(685, 0) * mm, "end": v(687.5, 10) * mm});
            skLineSegment(sketch, "E3.1.0.113", {"start": v(640, 0) * mm, "end": v(642.5, 10) * mm});
            skLineSegment(sketch, "E3.1.0.114", {"start": v(600, 0) * mm, "end": v(602.5, 10) * mm});
            skLineSegment(sketch, "E3.1.0.115", {"start": v(560, 0) * mm, "end": v(562.5, 10) * mm});
            skLineSegment(sketch, "E3.1.0.116", {"start": v(520, 0) * mm, "end": v(522.5, 10) * mm});
            skLineSegment(sketch, "E3.1.0.117", {"start": v(540, 0) * mm, "end": v(542.5, 10) * mm});
            skLineSegment(sketch, "E3.1.0.118", {"start": v(500, 0) * mm, "end": v(502.5, 10) * mm});
            skLineSegment(sketch, "E3.1.0.119", {"start": v(700, 0) * mm, "end": v(702.5, 10) * mm});
            skLineSegment(sketch, "E3.1.0.120", {"start": v(717.5, 10) * mm, "end": v(720, 0) * mm});
            skLineSegment(sketch, "E3.1.0.121", {"start": v(660, 0) * mm, "end": v(662.5, 10) * mm});
            skLineSegment(sketch, "E3.1.0.122", {"start": v(620, 0) * mm, "end": v(622.5, 10) * mm});
            skLineSegment(sketch, "E3.1.0.123", {"start": v(580, 0) * mm, "end": v(582.5, 10) * mm});
            skLineSegment(sketch, "E3.1.0.124", {"start": v(820, 0) * mm, "end": v(822.5, 10) * mm});
            skLineSegment(sketch, "E3.1.0.125", {"start": v(780, 0) * mm, "end": v(782.5, 10) * mm});
            skLineSegment(sketch, "E3.1.0.126", {"start": v(757.5, 10) * mm, "end": v(760, 0) * mm});
            skLineSegment(sketch, "E3.1.0.127", {"start": v(740, 0) * mm, "end": v(742.5, 10) * mm});
            skLineSegment(sketch, "E3.1.0.128", {"start": v(822.5, 10) * mm, "end": v(825, 0) * mm});
            skLineSegment(sketch, "E3.1.0.129", {"start": v(782.5, 10) * mm, "end": v(785, 0) * mm});
            skLineSegment(sketch, "E3.1.0.130", {"start": v(742.5, 10) * mm, "end": v(745, 0) * mm});
            skLineSegment(sketch, "E3.1.0.131", {"start": v(827.5, 10) * mm, "end": v(830, 0) * mm});
            skLineSegment(sketch, "E3.1.0.132", {"start": v(787.5, 10) * mm, "end": v(790, 0) * mm});
            skLineSegment(sketch, "E3.1.0.133", {"start": v(747.5, 10) * mm, "end": v(750, 0) * mm});
            skLineSegment(sketch, "E3.1.0.134", {"start": v(785, 0) * mm, "end": v(787.5, 10) * mm});
            skLineSegment(sketch, "E3.1.0.135", {"start": v(825, 0) * mm, "end": v(827.5, 10) * mm});
            skLineSegment(sketch, "E3.1.0.136", {"start": v(745, 0) * mm, "end": v(747.5, 10) * mm});
            skLineSegment(sketch, "E3.1.0.137", {"start": v(492.5, 10) * mm, "end": v(495, 0) * mm});
            skLineSegment(sketch, "E3.1.0.138", {"start": v(652.5, 10) * mm, "end": v(655, 0) * mm});
            skLineSegment(sketch, "E3.1.0.139", {"start": v(612.5, 10) * mm, "end": v(615, 0) * mm});
            skLineSegment(sketch, "E3.1.0.140", {"start": v(572.5, 10) * mm, "end": v(575, 0) * mm});
            skLineSegment(sketch, "E3.1.0.141", {"start": v(532.5, 10) * mm, "end": v(535, 0) * mm});
            skLineSegment(sketch, "E3.1.0.142", {"start": v(487.5, 10) * mm, "end": v(490, 0) * mm});
            skLineSegment(sketch, "E3.1.0.143", {"start": v(812.5, 10) * mm, "end": v(815, 0) * mm});
            skLineSegment(sketch, "E3.1.0.144", {"start": v(772.5, 10) * mm, "end": v(775, 0) * mm});
            skLineSegment(sketch, "E3.1.0.145", {"start": v(732.5, 10) * mm, "end": v(735, 0) * mm});
            skLineSegment(sketch, "E3.1.0.146", {"start": v(692.5, 10) * mm, "end": v(695, 0) * mm});
            skLineSegment(sketch, "E3.1.0.147", {"start": v(647.5, 10) * mm, "end": v(650, 0) * mm});
            skLineSegment(sketch, "E3.1.0.148", {"start": v(607.5, 10) * mm, "end": v(610, 0) * mm});
            skLineSegment(sketch, "E3.1.0.149", {"start": v(567.5, 10) * mm, "end": v(570, 0) * mm});
            skLineSegment(sketch, "E3.1.0.150", {"start": v(527.5, 10) * mm, "end": v(530, 0) * mm});
            skLineSegment(sketch, "E3.1.0.151", {"start": v(482.5, 10) * mm, "end": v(485, 0) * mm});
            skLineSegment(sketch, "E3.1.0.152", {"start": v(807.5, 10) * mm, "end": v(810, 0) * mm});
            skLineSegment(sketch, "E3.1.0.153", {"start": v(767.5, 10) * mm, "end": v(770, 0) * mm});
            skLineSegment(sketch, "E3.1.0.154", {"start": v(727.5, 10) * mm, "end": v(730, 0) * mm});
            skLineSegment(sketch, "E3.1.0.155", {"start": v(687.5, 10) * mm, "end": v(690, 0) * mm});
            skLineSegment(sketch, "E3.1.0.156", {"start": v(642.5, 10) * mm, "end": v(645, 0) * mm});
            skLineSegment(sketch, "E3.1.0.157", {"start": v(602.5, 10) * mm, "end": v(605, 0) * mm});
            skLineSegment(sketch, "E3.1.0.158", {"start": v(562.5, 10) * mm, "end": v(565, 0) * mm});
            skLineSegment(sketch, "E3.1.0.159", {"start": v(522.5, 10) * mm, "end": v(525, 0) * mm});
            skLineSegment(sketch, "E3.1.0.160", {"start": v(762.5, 10) * mm, "end": v(765, 0) * mm});
            skLineSegment(sketch, "E3.1.0.161", {"start": v(537.5, 10) * mm, "end": v(540, 0) * mm});
            skLineSegment(sketch, "E3.1.0.162", {"start": v(497.5, 10) * mm, "end": v(500, 0) * mm});
            skLineSegment(sketch, "E3.1.0.163", {"start": v(697.5, 10) * mm, "end": v(700, 0) * mm});
            skLineSegment(sketch, "E3.1.0.164", {"start": v(657.5, 10) * mm, "end": v(660, 0) * mm});
            skLineSegment(sketch, "E3.1.0.165", {"start": v(617.5, 10) * mm, "end": v(620, 0) * mm});
            skLineSegment(sketch, "E3.1.0.166", {"start": v(577.5, 10) * mm, "end": v(580, 0) * mm});
            skLineSegment(sketch, "E3.1.0.167", {"start": v(817.5, 10) * mm, "end": v(820, 0) * mm});
            skLineSegment(sketch, "E3.1.0.168", {"start": v(777.5, 10) * mm, "end": v(780, 0) * mm});
            skLineSegment(sketch, "E3.1.0.169", {"start": v(737.5, 10) * mm, "end": v(740, 0) * mm});
            skLineSegment(sketch, "E3.1.0.170", {"start": v(425, 0) * mm, "end": v(430, 0) * mm, "construction": true});
            skLineSegment(sketch, "E3.direction1", {"start": v(0, 0) * mm, "end": v(425, 0) * mm, "construction": true});
            skLineSegment(sketch, "E4", {"start": v(0, 0) * mm, "end": v(0, -15) * mm});
            skLineSegment(sketch, "E5", {"start": v(0, -15) * mm, "end": v(850, -15) * mm});
            skLineSegment(sketch, "E6", {"start": v(850, -15) * mm, "end": v(850, 0) * mm});
            skSolve(sketch);
        }
        {
            var Q0;
            Q0=makeQuery(id+"F0.imprint","IMPRINT",FACE,{"disambiguationData":[TD([[makeQuery(id+"F0.imprint","IMPRINT",EDGE,{"derivedFrom":sQuery(id+"F0.wireOp",EDGE,"E0")}),-1.0]])]});
            extrude(context, id + "F1", {"entities" : qUnion([Q0]), "depth" : 15 * mm, "offsetDistance" : 25 * mm});
        }
        {
            var Q0;
            Q0=makeQuery(id+"F1.opExtrude","CAP_FACE",FACE,{"disambiguationData":[OSD([sQuery(id+"F0.wireOp",EDGE,"E0"),sQuery(id+"F0.wireOp",EDGE,"E1"),sQuery(id+"F0.wireOp",EDGE,"E2.1.0.0"),sQuery(id+"F0.wireOp",EDGE,"E2.1.0.1"),sQuery(id+"F0.wireOp",EDGE,"E2.2.0.0"),sQuery(id+"F0.wireOp",EDGE,"E2.2.0.1"),sQuery(id+"F0.wireOp",EDGE,"E2.3.0.0"),sQuery(id+"F0.wireOp",EDGE,"E2.3.0.1"),sQuery(id+"F0.wireOp",EDGE,"E2.4.0.0"),sQuery(id+"F0.wireOp",EDGE,"E2.4.0.1"),sQuery(id+"F0.wireOp",EDGE,"E2.5.0.0"),sQuery(id+"F0.wireOp",EDGE,"E2.5.0.1"),sQuery(id+"F0.wireOp",EDGE,"E2.6.0.0"),sQuery(id+"F0.wireOp",EDGE,"E2.6.0.1"),sQuery(id+"F0.wireOp",EDGE,"E2.7.0.0"),sQuery(id+"F0.wireOp",EDGE,"E2.7.0.1"),sQuery(id+"F0.wireOp",EDGE,"E2.8.0.0"),sQuery(id+"F0.wireOp",EDGE,"E2.8.0.1"),sQuery(id+"F0.wireOp",EDGE,"E2.9.0.0"),sQuery(id+"F0.wireOp",EDGE,"E2.9.0.1"),sQuery(id+"F0.wireOp",EDGE,"E2.10.0.0"),sQuery(id+"F0.wireOp",EDGE,"E2.10.0.1"),sQuery(id+"F0.wireOp",EDGE,"E2.11.0.0"),sQuery(id+"F0.wireOp",EDGE,"E2.11.0.1"),sQuery(id+"F0.wireOp",EDGE,"E2.12.0.0"),sQuery(id+"F0.wireOp",EDGE,"E2.12.0.1"),sQuery(id+"F0.wireOp",EDGE,"E2.13.0.0"),sQuery(id+"F0.wireOp",EDGE,"E2.13.0.1"),sQuery(id+"F0.wireOp",EDGE,"E2.14.0.0"),sQuery(id+"F0.wireOp",EDGE,"E2.14.0.1"),sQuery(id+"F0.wireOp",EDGE,"E2.15.0.0"),sQuery(id+"F0.wireOp",EDGE,"E2.15.0.1"),sQuery(id+"F0.wireOp",EDGE,"E2.16.0.0"),sQuery(id+"F0.wireOp",EDGE,"E2.16.0.1"),sQuery(id+"F0.wireOp",EDGE,"E2.17.0.0"),sQuery(id+"F0.wireOp",EDGE,"E2.17.0.1"),sQuery(id+"F0.wireOp",EDGE,"E2.18.0.0"),sQuery(id+"F0.wireOp",EDGE,"E2.18.0.1"),sQuery(id+"F0.wireOp",EDGE,"E2.19.0.0"),sQuery(id+"F0.wireOp",EDGE,"E2.19.0.1"),sQuery(id+"F0.wireOp",EDGE,"E2.20.0.0"),sQuery(id+"F0.wireOp",EDGE,"E2.20.0.1"),sQuery(id+"F0.wireOp",EDGE,"E2.21.0.0"),sQuery(id+"F0.wireOp",EDGE,"E2.21.0.1"),sQuery(id+"F0.wireOp",EDGE,"E2.22.0.0"),sQuery(id+"F0.wireOp",EDGE,"E2.22.0.1"),sQuery(id+"F0.wireOp",EDGE,"E2.23.0.0"),sQuery(id+"F0.wireOp",EDGE,"E2.23.0.1"),sQuery(id+"F0.wireOp",EDGE,"E2.24.0.0"),sQuery(id+"F0.wireOp",EDGE,"E2.24.0.1"),sQuery(id+"F0.wireOp",EDGE,"E2.25.0.0"),sQuery(id+"F0.wireOp",EDGE,"E2.25.0.1"),sQuery(id+"F0.wireOp",EDGE,"E2.26.0.0"),sQuery(id+"F0.wireOp",EDGE,"E2.26.0.1"),sQuery(id+"F0.wireOp",EDGE,"E2.27.0.0"),sQuery(id+"F0.wireOp",EDGE,"E2.27.0.1"),sQuery(id+"F0.wireOp",EDGE,"E2.28.0.0"),sQuery(id+"F0.wireOp",EDGE,"E2.28.0.1"),sQuery(id+"F0.wireOp",EDGE,"E2.29.0.0"),sQuery(id+"F0.wireOp",EDGE,"E2.29.0.1"),sQuery(id+"F0.wireOp",EDGE,"E2.30.0.0"),sQuery(id+"F0.wireOp",EDGE,"E2.30.0.1"),sQuery(id+"F0.wireOp",EDGE,"E2.31.0.0"),sQuery(id+"F0.wireOp",EDGE,"E2.31.0.1"),sQuery(id+"F0.wireOp",EDGE,"E2.32.0.0"),sQuery(id+"F0.wireOp",EDGE,"E2.32.0.1"),sQuery(id+"F0.wireOp",EDGE,"E2.33.0.0"),sQuery(id+"F0.wireOp",EDGE,"E2.33.0.1"),sQuery(id+"F0.wireOp",EDGE,"E2.34.0.0"),sQuery(id+"F0.wireOp",EDGE,"E2.34.0.1"),sQuery(id+"F0.wireOp",EDGE,"E2.35.0.0"),sQuery(id+"F0.wireOp",EDGE,"E2.35.0.1"),sQuery(id+"F0.wireOp",EDGE,"E2.36.0.0"),sQuery(id+"F0.wireOp",EDGE,"E2.36.0.1"),sQuery(id+"F0.wireOp",EDGE,"E2.37.0.0"),sQuery(id+"F0.wireOp",EDGE,"E2.37.0.1"),sQuery(id+"F0.wireOp",EDGE,"E2.38.0.0"),sQuery(id+"F0.wireOp",EDGE,"E2.38.0.1"),sQuery(id+"F0.wireOp",EDGE,"E2.39.0.0"),sQuery(id+"F0.wireOp",EDGE,"E2.39.0.1"),sQuery(id+"F0.wireOp",EDGE,"E2.40.0.0"),sQuery(id+"F0.wireOp",EDGE,"E2.40.0.1"),sQuery(id+"F0.wireOp",EDGE,"E2.41.0.0"),sQuery(id+"F0.wireOp",EDGE,"E2.41.0.1"),sQuery(id+"F0.wireOp",EDGE,"E2.42.0.0"),sQuery(id+"F0.wireOp",EDGE,"E2.42.0.1"),sQuery(id+"F0.wireOp",EDGE,"E2.43.0.0"),sQuery(id+"F0.wireOp",EDGE,"E2.43.0.1"),sQuery(id+"F0.wireOp",EDGE,"E2.44.0.0"),sQuery(id+"F0.wireOp",EDGE,"E2.44.0.1"),sQuery(id+"F0.wireOp",EDGE,"E2.45.0.0"),sQuery(id+"F0.wireOp",EDGE,"E2.45.0.1"),sQuery(id+"F0.wireOp",EDGE,"E2.46.0.0"),sQuery(id+"F0.wireOp",EDGE,"E2.46.0.1"),sQuery(id+"F0.wireOp",EDGE,"E2.47.0.0"),sQuery(id+"F0.wireOp",EDGE,"E2.47.0.1"),sQuery(id+"F0.wireOp",EDGE,"E2.48.0.0"),sQuery(id+"F0.wireOp",EDGE,"E2.48.0.1"),sQuery(id+"F0.wireOp",EDGE,"E2.49.0.0"),sQuery(id+"F0.wireOp",EDGE,"E2.49.0.1"),sQuery(id+"F0.wireOp",EDGE,"E2.50.0.0"),sQuery(id+"F0.wireOp",EDGE,"E2.50.0.1"),sQuery(id+"F0.wireOp",EDGE,"E2.51.0.0"),sQuery(id+"F0.wireOp",EDGE,"E2.51.0.1"),sQuery(id+"F0.wireOp",EDGE,"E2.52.0.0"),sQuery(id+"F0.wireOp",EDGE,"E2.52.0.1"),sQuery(id+"F0.wireOp",EDGE,"E2.53.0.0"),sQuery(id+"F0.wireOp",EDGE,"E2.53.0.1"),sQuery(id+"F0.wireOp",EDGE,"E2.54.0.0"),sQuery(id+"F0.wireOp",EDGE,"E2.54.0.1"),sQuery(id+"F0.wireOp",EDGE,"E2.55.0.0"),sQuery(id+"F0.wireOp",EDGE,"E2.55.0.1"),sQuery(id+"F0.wireOp",EDGE,"E2.56.0.0"),sQuery(id+"F0.wireOp",EDGE,"E2.56.0.1"),sQuery(id+"F0.wireOp",EDGE,"E2.57.0.0"),sQuery(id+"F0.wireOp",EDGE,"E2.57.0.1"),sQuery(id+"F0.wireOp",EDGE,"E2.58.0.0"),sQuery(id+"F0.wireOp",EDGE,"E2.58.0.1"),sQuery(id+"F0.wireOp",EDGE,"E2.59.0.0"),sQuery(id+"F0.wireOp",EDGE,"E2.59.0.1"),sQuery(id+"F0.wireOp",EDGE,"E2.60.0.0"),sQuery(id+"F0.wireOp",EDGE,"E2.60.0.1"),sQuery(id+"F0.wireOp",EDGE,"E2.61.0.0"),sQuery(id+"F0.wireOp",EDGE,"E2.61.0.1"),sQuery(id+"F0.wireOp",EDGE,"E2.62.0.0"),sQuery(id+"F0.wireOp",EDGE,"E2.62.0.1"),sQuery(id+"F0.wireOp",EDGE,"E2.63.0.0"),sQuery(id+"F0.wireOp",EDGE,"E2.63.0.1"),sQuery(id+"F0.wireOp",EDGE,"E2.64.0.0"),sQuery(id+"F0.wireOp",EDGE,"E2.64.0.1"),sQuery(id+"F0.wireOp",EDGE,"E2.65.0.0"),sQuery(id+"F0.wireOp",EDGE,"E2.65.0.1"),sQuery(id+"F0.wireOp",EDGE,"E2.66.0.0"),sQuery(id+"F0.wireOp",EDGE,"E2.66.0.1"),sQuery(id+"F0.wireOp",EDGE,"E2.67.0.0"),sQuery(id+"F0.wireOp",EDGE,"E2.67.0.1"),sQuery(id+"F0.wireOp",EDGE,"E2.68.0.0"),sQuery(id+"F0.wireOp",EDGE,"E2.68.0.1"),sQuery(id+"F0.wireOp",EDGE,"E2.69.0.0"),sQuery(id+"F0.wireOp",EDGE,"E2.69.0.1"),sQuery(id+"F0.wireOp",EDGE,"E2.70.0.0"),sQuery(id+"F0.wireOp",EDGE,"E2.70.0.1"),sQuery(id+"F0.wireOp",EDGE,"E2.71.0.0"),sQuery(id+"F0.wireOp",EDGE,"E2.71.0.1"),sQuery(id+"F0.wireOp",EDGE,"E2.72.0.0"),sQuery(id+"F0.wireOp",EDGE,"E2.72.0.1"),sQuery(id+"F0.wireOp",EDGE,"E2.73.0.0"),sQuery(id+"F0.wireOp",EDGE,"E2.73.0.1"),sQuery(id+"F0.wireOp",EDGE,"E2.74.0.0"),sQuery(id+"F0.wireOp",EDGE,"E2.74.0.1"),sQuery(id+"F0.wireOp",EDGE,"E2.75.0.0"),sQuery(id+"F0.wireOp",EDGE,"E2.75.0.1"),sQuery(id+"F0.wireOp",EDGE,"E2.76.0.0"),sQuery(id+"F0.wireOp",EDGE,"E2.76.0.1"),sQuery(id+"F0.wireOp",EDGE,"E2.77.0.0"),sQuery(id+"F0.wireOp",EDGE,"E2.77.0.1"),sQuery(id+"F0.wireOp",EDGE,"E2.78.0.0"),sQuery(id+"F0.wireOp",EDGE,"E2.78.0.1"),sQuery(id+"F0.wireOp",EDGE,"E2.79.0.0"),sQuery(id+"F0.wireOp",EDGE,"E2.79.0.1"),sQuery(id+"F0.wireOp",EDGE,"E2.80.0.0"),sQuery(id+"F0.wireOp",EDGE,"E2.80.0.1"),sQuery(id+"F0.wireOp",EDGE,"E2.81.0.0"),sQuery(id+"F0.wireOp",EDGE,"E2.81.0.1"),sQuery(id+"F0.wireOp",EDGE,"E2.82.0.0"),sQuery(id+"F0.wireOp",EDGE,"E2.82.0.1"),sQuery(id+"F0.wireOp",EDGE,"E2.83.0.0"),sQuery(id+"F0.wireOp",EDGE,"E2.83.0.1"),sQuery(id+"F0.wireOp",EDGE,"E2.84.0.0"),sQuery(id+"F0.wireOp",EDGE,"E2.84.0.1"),sQuery(id+"F0.wireOp",EDGE,"E3.1.0.0"),sQuery(id+"F0.wireOp",EDGE,"E3.1.0.1"),sQuery(id+"F0.wireOp",EDGE,"E3.1.0.2"),sQuery(id+"F0.wireOp",EDGE,"E3.1.0.3"),sQuery(id+"F0.wireOp",EDGE,"E3.1.0.4"),sQuery(id+"F0.wireOp",EDGE,"E3.1.0.5"),sQuery(id+"F0.wireOp",EDGE,"E3.1.0.6"),sQuery(id+"F0.wireOp",EDGE,"E3.1.0.7"),sQuery(id+"F0.wireOp",EDGE,"E3.1.0.8"),sQuery(id+"F0.wireOp",EDGE,"E3.1.0.9"),sQuery(id+"F0.wireOp",EDGE,"E3.1.0.10"),sQuery(id+"F0.wireOp",EDGE,"E3.1.0.11"),sQuery(id+"F0.wireOp",EDGE,"E3.1.0.12"),sQuery(id+"F0.wireOp",EDGE,"E3.1.0.13"),sQuery(id+"F0.wireOp",EDGE,"E3.1.0.14"),sQuery(id+"F0.wireOp",EDGE,"E3.1.0.15"),sQuery(id+"F0.wireOp",EDGE,"E3.1.0.16"),sQuery(id+"F0.wireOp",EDGE,"E3.1.0.17"),sQuery(id+"F0.wireOp",EDGE,"E3.1.0.18"),sQuery(id+"F0.wireOp",EDGE,"E3.1.0.19"),sQuery(id+"F0.wireOp",EDGE,"E3.1.0.20"),sQuery(id+"F0.wireOp",EDGE,"E3.1.0.21"),sQuery(id+"F0.wireOp",EDGE,"E3.1.0.22"),sQuery(id+"F0.wireOp",EDGE,"E3.1.0.23"),sQuery(id+"F0.wireOp",EDGE,"E3.1.0.24"),sQuery(id+"F0.wireOp",EDGE,"E3.1.0.25"),sQuery(id+"F0.wireOp",EDGE,"E3.1.0.26"),sQuery(id+"F0.wireOp",EDGE,"E3.1.0.27"),sQuery(id+"F0.wireOp",EDGE,"E3.1.0.28"),sQuery(id+"F0.wireOp",EDGE,"E3.1.0.29"),sQuery(id+"F0.wireOp",EDGE,"E3.1.0.30"),sQuery(id+"F0.wireOp",EDGE,"E3.1.0.31"),sQuery(id+"F0.wireOp",EDGE,"E3.1.0.32"),sQuery(id+"F0.wireOp",EDGE,"E3.1.0.33"),sQuery(id+"F0.wireOp",EDGE,"E3.1.0.34"),sQuery(id+"F0.wireOp",EDGE,"E3.1.0.35"),sQuery(id+"F0.wireOp",EDGE,"E3.1.0.36"),sQuery(id+"F0.wireOp",EDGE,"E3.1.0.37"),sQuery(id+"F0.wireOp",EDGE,"E3.1.0.38"),sQuery(id+"F0.wireOp",EDGE,"E3.1.0.39"),sQuery(id+"F0.wireOp",EDGE,"E3.1.0.40"),sQuery(id+"F0.wireOp",EDGE,"E3.1.0.41"),sQuery(id+"F0.wireOp",EDGE,"E3.1.0.42"),sQuery(id+"F0.wireOp",EDGE,"E3.1.0.43"),sQuery(id+"F0.wireOp",EDGE,"E3.1.0.44"),sQuery(id+"F0.wireOp",EDGE,"E3.1.0.45"),sQuery(id+"F0.wireOp",EDGE,"E3.1.0.46"),sQuery(id+"F0.wireOp",EDGE,"E3.1.0.47"),sQuery(id+"F0.wireOp",EDGE,"E3.1.0.48"),sQuery(id+"F0.wireOp",EDGE,"E3.1.0.49"),sQuery(id+"F0.wireOp",EDGE,"E3.1.0.50"),sQuery(id+"F0.wireOp",EDGE,"E3.1.0.51"),sQuery(id+"F0.wireOp",EDGE,"E3.1.0.52"),sQuery(id+"F0.wireOp",EDGE,"E3.1.0.53"),sQuery(id+"F0.wireOp",EDGE,"E3.1.0.54"),sQuery(id+"F0.wireOp",EDGE,"E3.1.0.55"),sQuery(id+"F0.wireOp",EDGE,"E3.1.0.56"),sQuery(id+"F0.wireOp",EDGE,"E3.1.0.57"),sQuery(id+"F0.wireOp",EDGE,"E3.1.0.58"),sQuery(id+"F0.wireOp",EDGE,"E3.1.0.59"),sQuery(id+"F0.wireOp",EDGE,"E3.1.0.60"),sQuery(id+"F0.wireOp",EDGE,"E3.1.0.61"),sQuery(id+"F0.wireOp",EDGE,"E3.1.0.62"),sQuery(id+"F0.wireOp",EDGE,"E3.1.0.63"),sQuery(id+"F0.wireOp",EDGE,"E3.1.0.64"),sQuery(id+"F0.wireOp",EDGE,"E3.1.0.65"),sQuery(id+"F0.wireOp",EDGE,"E3.1.0.66"),sQuery(id+"F0.wireOp",EDGE,"E3.1.0.67"),sQuery(id+"F0.wireOp",EDGE,"E3.1.0.68"),sQuery(id+"F0.wireOp",EDGE,"E3.1.0.69"),sQuery(id+"F0.wireOp",EDGE,"E3.1.0.70"),sQuery(id+"F0.wireOp",EDGE,"E3.1.0.71"),sQuery(id+"F0.wireOp",EDGE,"E3.1.0.72"),sQuery(id+"F0.wireOp",EDGE,"E3.1.0.73"),sQuery(id+"F0.wireOp",EDGE,"E3.1.0.74"),sQuery(id+"F0.wireOp",EDGE,"E3.1.0.75"),sQuery(id+"F0.wireOp",EDGE,"E3.1.0.76"),sQuery(id+"F0.wireOp",EDGE,"E3.1.0.77"),sQuery(id+"F0.wireOp",EDGE,"E3.1.0.78"),sQuery(id+"F0.wireOp",EDGE,"E3.1.0.79"),sQuery(id+"F0.wireOp",EDGE,"E3.1.0.80"),sQuery(id+"F0.wireOp",EDGE,"E3.1.0.81"),sQuery(id+"F0.wireOp",EDGE,"E3.1.0.82"),sQuery(id+"F0.wireOp",EDGE,"E3.1.0.83"),sQuery(id+"F0.wireOp",EDGE,"E3.1.0.84"),sQuery(id+"F0.wireOp",EDGE,"E3.1.0.85"),sQuery(id+"F0.wireOp",EDGE,"E3.1.0.86"),sQuery(id+"F0.wireOp",EDGE,"E3.1.0.87"),sQuery(id+"F0.wireOp",EDGE,"E3.1.0.88"),sQuery(id+"F0.wireOp",EDGE,"E3.1.0.89"),sQuery(id+"F0.wireOp",EDGE,"E3.1.0.90"),sQuery(id+"F0.wireOp",EDGE,"E3.1.0.91"),sQuery(id+"F0.wireOp",EDGE,"E3.1.0.92"),sQuery(id+"F0.wireOp",EDGE,"E3.1.0.93"),sQuery(id+"F0.wireOp",EDGE,"E3.1.0.94"),sQuery(id+"F0.wireOp",EDGE,"E3.1.0.95"),sQuery(id+"F0.wireOp",EDGE,"E3.1.0.96"),sQuery(id+"F0.wireOp",EDGE,"E3.1.0.97"),sQuery(id+"F0.wireOp",EDGE,"E3.1.0.98"),sQuery(id+"F0.wireOp",EDGE,"E3.1.0.99"),sQuery(id+"F0.wireOp",EDGE,"E3.1.0.100"),sQuery(id+"F0.wireOp",EDGE,"E3.1.0.101"),sQuery(id+"F0.wireOp",EDGE,"E3.1.0.102"),sQuery(id+"F0.wireOp",EDGE,"E3.1.0.103"),sQuery(id+"F0.wireOp",EDGE,"E3.1.0.104"),sQuery(id+"F0.wireOp",EDGE,"E3.1.0.105"),sQuery(id+"F0.wireOp",EDGE,"E3.1.0.106"),sQuery(id+"F0.wireOp",EDGE,"E3.1.0.107"),sQuery(id+"F0.wireOp",EDGE,"E3.1.0.108"),sQuery(id+"F0.wireOp",EDGE,"E3.1.0.109"),sQuery(id+"F0.wireOp",EDGE,"E3.1.0.110"),sQuery(id+"F0.wireOp",EDGE,"E3.1.0.111"),sQuery(id+"F0.wireOp",EDGE,"E3.1.0.112"),sQuery(id+"F0.wireOp",EDGE,"E3.1.0.113"),sQuery(id+"F0.wireOp",EDGE,"E3.1.0.114"),sQuery(id+"F0.wireOp",EDGE,"E3.1.0.115"),sQuery(id+"F0.wireOp",EDGE,"E3.1.0.116"),sQuery(id+"F0.wireOp",EDGE,"E3.1.0.117"),sQuery(id+"F0.wireOp",EDGE,"E3.1.0.118"),sQuery(id+"F0.wireOp",EDGE,"E3.1.0.119"),sQuery(id+"F0.wireOp",EDGE,"E3.1.0.120"),sQuery(id+"F0.wireOp",EDGE,"E3.1.0.121"),sQuery(id+"F0.wireOp",EDGE,"E3.1.0.122"),sQuery(id+"F0.wireOp",EDGE,"E3.1.0.123"),sQuery(id+"F0.wireOp",EDGE,"E3.1.0.124"),sQuery(id+"F0.wireOp",EDGE,"E3.1.0.125"),sQuery(id+"F0.wireOp",EDGE,"E3.1.0.126"),sQuery(id+"F0.wireOp",EDGE,"E3.1.0.127"),sQuery(id+"F0.wireOp",EDGE,"E3.1.0.128"),sQuery(id+"F0.wireOp",EDGE,"E3.1.0.129"),sQuery(id+"F0.wireOp",EDGE,"E3.1.0.130"),sQuery(id+"F0.wireOp",EDGE,"E3.1.0.131"),sQuery(id+"F0.wireOp",EDGE,"E3.1.0.132"),sQuery(id+"F0.wireOp",EDGE,"E3.1.0.133"),sQuery(id+"F0.wireOp",EDGE,"E3.1.0.134"),sQuery(id+"F0.wireOp",EDGE,"E3.1.0.135"),sQuery(id+"F0.wireOp",EDGE,"E3.1.0.136"),sQuery(id+"F0.wireOp",EDGE,"E3.1.0.137"),sQuery(id+"F0.wireOp",EDGE,"E3.1.0.138"),sQuery(id+"F0.wireOp",EDGE,"E3.1.0.139"),sQuery(id+"F0.wireOp",EDGE,"E3.1.0.140"),sQuery(id+"F0.wireOp",EDGE,"E3.1.0.141"),sQuery(id+"F0.wireOp",EDGE,"E3.1.0.142"),sQuery(id+"F0.wireOp",EDGE,"E3.1.0.143"),sQuery(id+"F0.wireOp",EDGE,"E3.1.0.144"),sQuery(id+"F0.wireOp",EDGE,"E3.1.0.145"),sQuery(id+"F0.wireOp",EDGE,"E3.1.0.146"),sQuery(id+"F0.wireOp",EDGE,"E3.1.0.147"),sQuery(id+"F0.wireOp",EDGE,"E3.1.0.148"),sQuery(id+"F0.wireOp",EDGE,"E3.1.0.149"),sQuery(id+"F0.wireOp",EDGE,"E3.1.0.150"),sQuery(id+"F0.wireOp",EDGE,"E3.1.0.151"),sQuery(id+"F0.wireOp",EDGE,"E3.1.0.152"),sQuery(id+"F0.wireOp",EDGE,"E3.1.0.153"),sQuery(id+"F0.wireOp",EDGE,"E3.1.0.154"),sQuery(id+"F0.wireOp",EDGE,"E3.1.0.155"),sQuery(id+"F0.wireOp",EDGE,"E3.1.0.156"),sQuery(id+"F0.wireOp",EDGE,"E3.1.0.157"),sQuery(id+"F0.wireOp",EDGE,"E3.1.0.158"),sQuery(id+"F0.wireOp",EDGE,"E3.1.0.159"),sQuery(id+"F0.wireOp",EDGE,"E3.1.0.160"),sQuery(id+"F0.wireOp",EDGE,"E3.1.0.161"),sQuery(id+"F0.wireOp",EDGE,"E3.1.0.162"),sQuery(id+"F0.wireOp",EDGE,"E3.1.0.163"),sQuery(id+"F0.wireOp",EDGE,"E3.1.0.164"),sQuery(id+"F0.wireOp",EDGE,"E3.1.0.165"),sQuery(id+"F0.wireOp",EDGE,"E3.1.0.166"),sQuery(id+"F0.wireOp",EDGE,"E3.1.0.167"),sQuery(id+"F0.wireOp",EDGE,"E3.1.0.168"),sQuery(id+"F0.wireOp",EDGE,"E3.1.0.169"),sQuery(id+"F0.wireOp",EDGE,"E4"),sQuery(id+"F0.wireOp",EDGE,"E5"),sQuery(id+"F0.wireOp",EDGE,"E6")])],"isStart":false});
            var sketch = newSketch(context, id + "F2", { "sketchPlane" : qUnion([Q0])});
            skPoint(sketch, "E7", {"position": v(25, -7.5) * mm});
            skPoint(sketch, "E7.positionSnap0", {"position": v(0, -7.5) * mm});
            skPoint(sketch, "E8", {"position": v(425, -7.5) * mm});
            skPoint(sketch, "E9", {"position": v(625, -7.5) * mm});
            skPoint(sketch, "E10", {"position": v(825, -7.5) * mm});
            skLineSegment(sketch, "E11", {"start": v(0, -7.5) * mm, "end": v(25, -7.5) * mm, "construction": true});
            skLineSegment(sketch, "E12", {"start": v(425, -7.5) * mm, "end": v(625, -7.5) * mm, "construction": true});
            skLineSegment(sketch, "E13", {"start": v(625, -7.5) * mm, "end": v(825, -7.5) * mm, "construction": true});
            skLineSegment(sketch, "E14", {"start": v(825, -7.5) * mm, "end": v(850, -7.5) * mm, "construction": true});
            skPoint(sketch, "E15", {"position": v(225, -7.5) * mm});
            skLineSegment(sketch, "E16", {"start": v(25, -7.5) * mm, "end": v(225, -7.5) * mm, "construction": true});
            skLineSegment(sketch, "E17", {"start": v(225, -7.5) * mm, "end": v(425, -7.5) * mm, "construction": true});
            skSolve(sketch);
        }
        {
            var Q0;
            Q0=sQuery(id+"F2.wireOp",VERTEX,"E7");
            var Q1;
            Q1=sQuery(id+"F2.wireOp",VERTEX,"E15");
            var Q2;
            Q2=sQuery(id+"F2.wireOp",VERTEX,"E8");
            var Q3;
            Q3=sQuery(id+"F2.wireOp",VERTEX,"E9");
            var Q4;
            Q4=sQuery(id+"F2.wireOp",VERTEX,"E10");
            var Q5;
            Q5=makeQuery(id+"F1.opExtrude","SWEPT_BODY",BODY,{"disambiguationData":[OSD([sQuery(id+"F0.wireOp",EDGE,"E0"),sQuery(id+"F0.wireOp",EDGE,"E1"),sQuery(id+"F0.wireOp",EDGE,"E2.1.0.0"),sQuery(id+"F0.wireOp",EDGE,"E2.1.0.1"),sQuery(id+"F0.wireOp",EDGE,"E2.2.0.0"),sQuery(id+"F0.wireOp",EDGE,"E2.2.0.1"),sQuery(id+"F0.wireOp",EDGE,"E2.3.0.0"),sQuery(id+"F0.wireOp",EDGE,"E2.3.0.1"),sQuery(id+"F0.wireOp",EDGE,"E2.4.0.0"),sQuery(id+"F0.wireOp",EDGE,"E2.4.0.1"),sQuery(id+"F0.wireOp",EDGE,"E2.5.0.0"),sQuery(id+"F0.wireOp",EDGE,"E2.5.0.1"),sQuery(id+"F0.wireOp",EDGE,"E2.6.0.0"),sQuery(id+"F0.wireOp",EDGE,"E2.6.0.1"),sQuery(id+"F0.wireOp",EDGE,"E2.7.0.0"),sQuery(id+"F0.wireOp",EDGE,"E2.7.0.1"),sQuery(id+"F0.wireOp",EDGE,"E2.8.0.0"),sQuery(id+"F0.wireOp",EDGE,"E2.8.0.1"),sQuery(id+"F0.wireOp",EDGE,"E2.9.0.0"),sQuery(id+"F0.wireOp",EDGE,"E2.9.0.1"),sQuery(id+"F0.wireOp",EDGE,"E2.10.0.0"),sQuery(id+"F0.wireOp",EDGE,"E2.10.0.1"),sQuery(id+"F0.wireOp",EDGE,"E2.11.0.0"),sQuery(id+"F0.wireOp",EDGE,"E2.11.0.1"),sQuery(id+"F0.wireOp",EDGE,"E2.12.0.0"),sQuery(id+"F0.wireOp",EDGE,"E2.12.0.1"),sQuery(id+"F0.wireOp",EDGE,"E2.13.0.0"),sQuery(id+"F0.wireOp",EDGE,"E2.13.0.1"),sQuery(id+"F0.wireOp",EDGE,"E2.14.0.0"),sQuery(id+"F0.wireOp",EDGE,"E2.14.0.1"),sQuery(id+"F0.wireOp",EDGE,"E2.15.0.0"),sQuery(id+"F0.wireOp",EDGE,"E2.15.0.1"),sQuery(id+"F0.wireOp",EDGE,"E2.16.0.0"),sQuery(id+"F0.wireOp",EDGE,"E2.16.0.1"),sQuery(id+"F0.wireOp",EDGE,"E2.17.0.0"),sQuery(id+"F0.wireOp",EDGE,"E2.17.0.1"),sQuery(id+"F0.wireOp",EDGE,"E2.18.0.0"),sQuery(id+"F0.wireOp",EDGE,"E2.18.0.1"),sQuery(id+"F0.wireOp",EDGE,"E2.19.0.0"),sQuery(id+"F0.wireOp",EDGE,"E2.19.0.1"),sQuery(id+"F0.wireOp",EDGE,"E2.20.0.0"),sQuery(id+"F0.wireOp",EDGE,"E2.20.0.1"),sQuery(id+"F0.wireOp",EDGE,"E2.21.0.0"),sQuery(id+"F0.wireOp",EDGE,"E2.21.0.1"),sQuery(id+"F0.wireOp",EDGE,"E2.22.0.0"),sQuery(id+"F0.wireOp",EDGE,"E2.22.0.1"),sQuery(id+"F0.wireOp",EDGE,"E2.23.0.0"),sQuery(id+"F0.wireOp",EDGE,"E2.23.0.1"),sQuery(id+"F0.wireOp",EDGE,"E2.24.0.0"),sQuery(id+"F0.wireOp",EDGE,"E2.24.0.1"),sQuery(id+"F0.wireOp",EDGE,"E2.25.0.0"),sQuery(id+"F0.wireOp",EDGE,"E2.25.0.1"),sQuery(id+"F0.wireOp",EDGE,"E2.26.0.0"),sQuery(id+"F0.wireOp",EDGE,"E2.26.0.1"),sQuery(id+"F0.wireOp",EDGE,"E2.27.0.0"),sQuery(id+"F0.wireOp",EDGE,"E2.27.0.1"),sQuery(id+"F0.wireOp",EDGE,"E2.28.0.0"),sQuery(id+"F0.wireOp",EDGE,"E2.28.0.1"),sQuery(id+"F0.wireOp",EDGE,"E2.29.0.0"),sQuery(id+"F0.wireOp",EDGE,"E2.29.0.1"),sQuery(id+"F0.wireOp",EDGE,"E2.30.0.0"),sQuery(id+"F0.wireOp",EDGE,"E2.30.0.1"),sQuery(id+"F0.wireOp",EDGE,"E2.31.0.0"),sQuery(id+"F0.wireOp",EDGE,"E2.31.0.1"),sQuery(id+"F0.wireOp",EDGE,"E2.32.0.0"),sQuery(id+"F0.wireOp",EDGE,"E2.32.0.1"),sQuery(id+"F0.wireOp",EDGE,"E2.33.0.0"),sQuery(id+"F0.wireOp",EDGE,"E2.33.0.1"),sQuery(id+"F0.wireOp",EDGE,"E2.34.0.0"),sQuery(id+"F0.wireOp",EDGE,"E2.34.0.1"),sQuery(id+"F0.wireOp",EDGE,"E2.35.0.0"),sQuery(id+"F0.wireOp",EDGE,"E2.35.0.1"),sQuery(id+"F0.wireOp",EDGE,"E2.36.0.0"),sQuery(id+"F0.wireOp",EDGE,"E2.36.0.1"),sQuery(id+"F0.wireOp",EDGE,"E2.37.0.0"),sQuery(id+"F0.wireOp",EDGE,"E2.37.0.1"),sQuery(id+"F0.wireOp",EDGE,"E2.38.0.0"),sQuery(id+"F0.wireOp",EDGE,"E2.38.0.1"),sQuery(id+"F0.wireOp",EDGE,"E2.39.0.0"),sQuery(id+"F0.wireOp",EDGE,"E2.39.0.1"),sQuery(id+"F0.wireOp",EDGE,"E2.40.0.0"),sQuery(id+"F0.wireOp",EDGE,"E2.40.0.1"),sQuery(id+"F0.wireOp",EDGE,"E2.41.0.0"),sQuery(id+"F0.wireOp",EDGE,"E2.41.0.1"),sQuery(id+"F0.wireOp",EDGE,"E2.42.0.0"),sQuery(id+"F0.wireOp",EDGE,"E2.42.0.1"),sQuery(id+"F0.wireOp",EDGE,"E2.43.0.0"),sQuery(id+"F0.wireOp",EDGE,"E2.43.0.1"),sQuery(id+"F0.wireOp",EDGE,"E2.44.0.0"),sQuery(id+"F0.wireOp",EDGE,"E2.44.0.1"),sQuery(id+"F0.wireOp",EDGE,"E2.45.0.0"),sQuery(id+"F0.wireOp",EDGE,"E2.45.0.1"),sQuery(id+"F0.wireOp",EDGE,"E2.46.0.0"),sQuery(id+"F0.wireOp",EDGE,"E2.46.0.1"),sQuery(id+"F0.wireOp",EDGE,"E2.47.0.0"),sQuery(id+"F0.wireOp",EDGE,"E2.47.0.1"),sQuery(id+"F0.wireOp",EDGE,"E2.48.0.0"),sQuery(id+"F0.wireOp",EDGE,"E2.48.0.1"),sQuery(id+"F0.wireOp",EDGE,"E2.49.0.0"),sQuery(id+"F0.wireOp",EDGE,"E2.49.0.1"),sQuery(id+"F0.wireOp",EDGE,"E2.50.0.0"),sQuery(id+"F0.wireOp",EDGE,"E2.50.0.1"),sQuery(id+"F0.wireOp",EDGE,"E2.51.0.0"),sQuery(id+"F0.wireOp",EDGE,"E2.51.0.1"),sQuery(id+"F0.wireOp",EDGE,"E2.52.0.0"),sQuery(id+"F0.wireOp",EDGE,"E2.52.0.1"),sQuery(id+"F0.wireOp",EDGE,"E2.53.0.0"),sQuery(id+"F0.wireOp",EDGE,"E2.53.0.1"),sQuery(id+"F0.wireOp",EDGE,"E2.54.0.0"),sQuery(id+"F0.wireOp",EDGE,"E2.54.0.1"),sQuery(id+"F0.wireOp",EDGE,"E2.55.0.0"),sQuery(id+"F0.wireOp",EDGE,"E2.55.0.1"),sQuery(id+"F0.wireOp",EDGE,"E2.56.0.0"),sQuery(id+"F0.wireOp",EDGE,"E2.56.0.1"),sQuery(id+"F0.wireOp",EDGE,"E2.57.0.0"),sQuery(id+"F0.wireOp",EDGE,"E2.57.0.1"),sQuery(id+"F0.wireOp",EDGE,"E2.58.0.0"),sQuery(id+"F0.wireOp",EDGE,"E2.58.0.1"),sQuery(id+"F0.wireOp",EDGE,"E2.59.0.0"),sQuery(id+"F0.wireOp",EDGE,"E2.59.0.1"),sQuery(id+"F0.wireOp",EDGE,"E2.60.0.0"),sQuery(id+"F0.wireOp",EDGE,"E2.60.0.1"),sQuery(id+"F0.wireOp",EDGE,"E2.61.0.0"),sQuery(id+"F0.wireOp",EDGE,"E2.61.0.1"),sQuery(id+"F0.wireOp",EDGE,"E2.62.0.0"),sQuery(id+"F0.wireOp",EDGE,"E2.62.0.1"),sQuery(id+"F0.wireOp",EDGE,"E2.63.0.0"),sQuery(id+"F0.wireOp",EDGE,"E2.63.0.1"),sQuery(id+"F0.wireOp",EDGE,"E2.64.0.0"),sQuery(id+"F0.wireOp",EDGE,"E2.64.0.1"),sQuery(id+"F0.wireOp",EDGE,"E2.65.0.0"),sQuery(id+"F0.wireOp",EDGE,"E2.65.0.1"),sQuery(id+"F0.wireOp",EDGE,"E2.66.0.0"),sQuery(id+"F0.wireOp",EDGE,"E2.66.0.1"),sQuery(id+"F0.wireOp",EDGE,"E2.67.0.0"),sQuery(id+"F0.wireOp",EDGE,"E2.67.0.1"),sQuery(id+"F0.wireOp",EDGE,"E2.68.0.0"),sQuery(id+"F0.wireOp",EDGE,"E2.68.0.1"),sQuery(id+"F0.wireOp",EDGE,"E2.69.0.0"),sQuery(id+"F0.wireOp",EDGE,"E2.69.0.1"),sQuery(id+"F0.wireOp",EDGE,"E2.70.0.0"),sQuery(id+"F0.wireOp",EDGE,"E2.70.0.1"),sQuery(id+"F0.wireOp",EDGE,"E2.71.0.0"),sQuery(id+"F0.wireOp",EDGE,"E2.71.0.1"),sQuery(id+"F0.wireOp",EDGE,"E2.72.0.0"),sQuery(id+"F0.wireOp",EDGE,"E2.72.0.1"),sQuery(id+"F0.wireOp",EDGE,"E2.73.0.0"),sQuery(id+"F0.wireOp",EDGE,"E2.73.0.1"),sQuery(id+"F0.wireOp",EDGE,"E2.74.0.0"),sQuery(id+"F0.wireOp",EDGE,"E2.74.0.1"),sQuery(id+"F0.wireOp",EDGE,"E2.75.0.0"),sQuery(id+"F0.wireOp",EDGE,"E2.75.0.1"),sQuery(id+"F0.wireOp",EDGE,"E2.76.0.0"),sQuery(id+"F0.wireOp",EDGE,"E2.76.0.1"),sQuery(id+"F0.wireOp",EDGE,"E2.77.0.0"),sQuery(id+"F0.wireOp",EDGE,"E2.77.0.1"),sQuery(id+"F0.wireOp",EDGE,"E2.78.0.0"),sQuery(id+"F0.wireOp",EDGE,"E2.78.0.1"),sQuery(id+"F0.wireOp",EDGE,"E2.79.0.0"),sQuery(id+"F0.wireOp",EDGE,"E2.79.0.1"),sQuery(id+"F0.wireOp",EDGE,"E2.80.0.0"),sQuery(id+"F0.wireOp",EDGE,"E2.80.0.1"),sQuery(id+"F0.wireOp",EDGE,"E2.81.0.0"),sQuery(id+"F0.wireOp",EDGE,"E2.81.0.1"),sQuery(id+"F0.wireOp",EDGE,"E2.82.0.0"),sQuery(id+"F0.wireOp",EDGE,"E2.82.0.1"),sQuery(id+"F0.wireOp",EDGE,"E2.83.0.0"),sQuery(id+"F0.wireOp",EDGE,"E2.83.0.1"),sQuery(id+"F0.wireOp",EDGE,"E2.84.0.0"),sQuery(id+"F0.wireOp",EDGE,"E2.84.0.1"),sQuery(id+"F0.wireOp",EDGE,"E3.1.0.0"),sQuery(id+"F0.wireOp",EDGE,"E3.1.0.1"),sQuery(id+"F0.wireOp",EDGE,"E3.1.0.2"),sQuery(id+"F0.wireOp",EDGE,"E3.1.0.3"),sQuery(id+"F0.wireOp",EDGE,"E3.1.0.4"),sQuery(id+"F0.wireOp",EDGE,"E3.1.0.5"),sQuery(id+"F0.wireOp",EDGE,"E3.1.0.6"),sQuery(id+"F0.wireOp",EDGE,"E3.1.0.7"),sQuery(id+"F0.wireOp",EDGE,"E3.1.0.8"),sQuery(id+"F0.wireOp",EDGE,"E3.1.0.9"),sQuery(id+"F0.wireOp",EDGE,"E3.1.0.10"),sQuery(id+"F0.wireOp",EDGE,"E3.1.0.11"),sQuery(id+"F0.wireOp",EDGE,"E3.1.0.12"),sQuery(id+"F0.wireOp",EDGE,"E3.1.0.13"),sQuery(id+"F0.wireOp",EDGE,"E3.1.0.14"),sQuery(id+"F0.wireOp",EDGE,"E3.1.0.15"),sQuery(id+"F0.wireOp",EDGE,"E3.1.0.16"),sQuery(id+"F0.wireOp",EDGE,"E3.1.0.17"),sQuery(id+"F0.wireOp",EDGE,"E3.1.0.18"),sQuery(id+"F0.wireOp",EDGE,"E3.1.0.19"),sQuery(id+"F0.wireOp",EDGE,"E3.1.0.20"),sQuery(id+"F0.wireOp",EDGE,"E3.1.0.21"),sQuery(id+"F0.wireOp",EDGE,"E3.1.0.22"),sQuery(id+"F0.wireOp",EDGE,"E3.1.0.23"),sQuery(id+"F0.wireOp",EDGE,"E3.1.0.24"),sQuery(id+"F0.wireOp",EDGE,"E3.1.0.25"),sQuery(id+"F0.wireOp",EDGE,"E3.1.0.26"),sQuery(id+"F0.wireOp",EDGE,"E3.1.0.27"),sQuery(id+"F0.wireOp",EDGE,"E3.1.0.28"),sQuery(id+"F0.wireOp",EDGE,"E3.1.0.29"),sQuery(id+"F0.wireOp",EDGE,"E3.1.0.30"),sQuery(id+"F0.wireOp",EDGE,"E3.1.0.31"),sQuery(id+"F0.wireOp",EDGE,"E3.1.0.32"),sQuery(id+"F0.wireOp",EDGE,"E3.1.0.33"),sQuery(id+"F0.wireOp",EDGE,"E3.1.0.34"),sQuery(id+"F0.wireOp",EDGE,"E3.1.0.35"),sQuery(id+"F0.wireOp",EDGE,"E3.1.0.36"),sQuery(id+"F0.wireOp",EDGE,"E3.1.0.37"),sQuery(id+"F0.wireOp",EDGE,"E3.1.0.38"),sQuery(id+"F0.wireOp",EDGE,"E3.1.0.39"),sQuery(id+"F0.wireOp",EDGE,"E3.1.0.40"),sQuery(id+"F0.wireOp",EDGE,"E3.1.0.41"),sQuery(id+"F0.wireOp",EDGE,"E3.1.0.42"),sQuery(id+"F0.wireOp",EDGE,"E3.1.0.43"),sQuery(id+"F0.wireOp",EDGE,"E3.1.0.44"),sQuery(id+"F0.wireOp",EDGE,"E3.1.0.45"),sQuery(id+"F0.wireOp",EDGE,"E3.1.0.46"),sQuery(id+"F0.wireOp",EDGE,"E3.1.0.47"),sQuery(id+"F0.wireOp",EDGE,"E3.1.0.48"),sQuery(id+"F0.wireOp",EDGE,"E3.1.0.49"),sQuery(id+"F0.wireOp",EDGE,"E3.1.0.50"),sQuery(id+"F0.wireOp",EDGE,"E3.1.0.51"),sQuery(id+"F0.wireOp",EDGE,"E3.1.0.52"),sQuery(id+"F0.wireOp",EDGE,"E3.1.0.53"),sQuery(id+"F0.wireOp",EDGE,"E3.1.0.54"),sQuery(id+"F0.wireOp",EDGE,"E3.1.0.55"),sQuery(id+"F0.wireOp",EDGE,"E3.1.0.56"),sQuery(id+"F0.wireOp",EDGE,"E3.1.0.57"),sQuery(id+"F0.wireOp",EDGE,"E3.1.0.58"),sQuery(id+"F0.wireOp",EDGE,"E3.1.0.59"),sQuery(id+"F0.wireOp",EDGE,"E3.1.0.60"),sQuery(id+"F0.wireOp",EDGE,"E3.1.0.61"),sQuery(id+"F0.wireOp",EDGE,"E3.1.0.62"),sQuery(id+"F0.wireOp",EDGE,"E3.1.0.63"),sQuery(id+"F0.wireOp",EDGE,"E3.1.0.64"),sQuery(id+"F0.wireOp",EDGE,"E3.1.0.65"),sQuery(id+"F0.wireOp",EDGE,"E3.1.0.66"),sQuery(id+"F0.wireOp",EDGE,"E3.1.0.67"),sQuery(id+"F0.wireOp",EDGE,"E3.1.0.68"),sQuery(id+"F0.wireOp",EDGE,"E3.1.0.69"),sQuery(id+"F0.wireOp",EDGE,"E3.1.0.70"),sQuery(id+"F0.wireOp",EDGE,"E3.1.0.71"),sQuery(id+"F0.wireOp",EDGE,"E3.1.0.72"),sQuery(id+"F0.wireOp",EDGE,"E3.1.0.73"),sQuery(id+"F0.wireOp",EDGE,"E3.1.0.74"),sQuery(id+"F0.wireOp",EDGE,"E3.1.0.75"),sQuery(id+"F0.wireOp",EDGE,"E3.1.0.76"),sQuery(id+"F0.wireOp",EDGE,"E3.1.0.77"),sQuery(id+"F0.wireOp",EDGE,"E3.1.0.78"),sQuery(id+"F0.wireOp",EDGE,"E3.1.0.79"),sQuery(id+"F0.wireOp",EDGE,"E3.1.0.80"),sQuery(id+"F0.wireOp",EDGE,"E3.1.0.81"),sQuery(id+"F0.wireOp",EDGE,"E3.1.0.82"),sQuery(id+"F0.wireOp",EDGE,"E3.1.0.83"),sQuery(id+"F0.wireOp",EDGE,"E3.1.0.84"),sQuery(id+"F0.wireOp",EDGE,"E3.1.0.85"),sQuery(id+"F0.wireOp",EDGE,"E3.1.0.86"),sQuery(id+"F0.wireOp",EDGE,"E3.1.0.87"),sQuery(id+"F0.wireOp",EDGE,"E3.1.0.88"),sQuery(id+"F0.wireOp",EDGE,"E3.1.0.89"),sQuery(id+"F0.wireOp",EDGE,"E3.1.0.90"),sQuery(id+"F0.wireOp",EDGE,"E3.1.0.91"),sQuery(id+"F0.wireOp",EDGE,"E3.1.0.92"),sQuery(id+"F0.wireOp",EDGE,"E3.1.0.93"),sQuery(id+"F0.wireOp",EDGE,"E3.1.0.94"),sQuery(id+"F0.wireOp",EDGE,"E3.1.0.95"),sQuery(id+"F0.wireOp",EDGE,"E3.1.0.96"),sQuery(id+"F0.wireOp",EDGE,"E3.1.0.97"),sQuery(id+"F0.wireOp",EDGE,"E3.1.0.98"),sQuery(id+"F0.wireOp",EDGE,"E3.1.0.99"),sQuery(id+"F0.wireOp",EDGE,"E3.1.0.100"),sQuery(id+"F0.wireOp",EDGE,"E3.1.0.101"),sQuery(id+"F0.wireOp",EDGE,"E3.1.0.102"),sQuery(id+"F0.wireOp",EDGE,"E3.1.0.103"),sQuery(id+"F0.wireOp",EDGE,"E3.1.0.104"),sQuery(id+"F0.wireOp",EDGE,"E3.1.0.105"),sQuery(id+"F0.wireOp",EDGE,"E3.1.0.106"),sQuery(id+"F0.wireOp",EDGE,"E3.1.0.107"),sQuery(id+"F0.wireOp",EDGE,"E3.1.0.108"),sQuery(id+"F0.wireOp",EDGE,"E3.1.0.109"),sQuery(id+"F0.wireOp",EDGE,"E3.1.0.110"),sQuery(id+"F0.wireOp",EDGE,"E3.1.0.111"),sQuery(id+"F0.wireOp",EDGE,"E3.1.0.112"),sQuery(id+"F0.wireOp",EDGE,"E3.1.0.113"),sQuery(id+"F0.wireOp",EDGE,"E3.1.0.114"),sQuery(id+"F0.wireOp",EDGE,"E3.1.0.115"),sQuery(id+"F0.wireOp",EDGE,"E3.1.0.116"),sQuery(id+"F0.wireOp",EDGE,"E3.1.0.117"),sQuery(id+"F0.wireOp",EDGE,"E3.1.0.118"),sQuery(id+"F0.wireOp",EDGE,"E3.1.0.119"),sQuery(id+"F0.wireOp",EDGE,"E3.1.0.120"),sQuery(id+"F0.wireOp",EDGE,"E3.1.0.121"),sQuery(id+"F0.wireOp",EDGE,"E3.1.0.122"),sQuery(id+"F0.wireOp",EDGE,"E3.1.0.123"),sQuery(id+"F0.wireOp",EDGE,"E3.1.0.124"),sQuery(id+"F0.wireOp",EDGE,"E3.1.0.125"),sQuery(id+"F0.wireOp",EDGE,"E3.1.0.126"),sQuery(id+"F0.wireOp",EDGE,"E3.1.0.127"),sQuery(id+"F0.wireOp",EDGE,"E3.1.0.128"),sQuery(id+"F0.wireOp",EDGE,"E3.1.0.129"),sQuery(id+"F0.wireOp",EDGE,"E3.1.0.130"),sQuery(id+"F0.wireOp",EDGE,"E3.1.0.131"),sQuery(id+"F0.wireOp",EDGE,"E3.1.0.132"),sQuery(id+"F0.wireOp",EDGE,"E3.1.0.133"),sQuery(id+"F0.wireOp",EDGE,"E3.1.0.134"),sQuery(id+"F0.wireOp",EDGE,"E3.1.0.135"),sQuery(id+"F0.wireOp",EDGE,"E3.1.0.136"),sQuery(id+"F0.wireOp",EDGE,"E3.1.0.137"),sQuery(id+"F0.wireOp",EDGE,"E3.1.0.138"),sQuery(id+"F0.wireOp",EDGE,"E3.1.0.139"),sQuery(id+"F0.wireOp",EDGE,"E3.1.0.140"),sQuery(id+"F0.wireOp",EDGE,"E3.1.0.141"),sQuery(id+"F0.wireOp",EDGE,"E3.1.0.142"),sQuery(id+"F0.wireOp",EDGE,"E3.1.0.143"),sQuery(id+"F0.wireOp",EDGE,"E3.1.0.144"),sQuery(id+"F0.wireOp",EDGE,"E3.1.0.145"),sQuery(id+"F0.wireOp",EDGE,"E3.1.0.146"),sQuery(id+"F0.wireOp",EDGE,"E3.1.0.147"),sQuery(id+"F0.wireOp",EDGE,"E3.1.0.148"),sQuery(id+"F0.wireOp",EDGE,"E3.1.0.149"),sQuery(id+"F0.wireOp",EDGE,"E3.1.0.150"),sQuery(id+"F0.wireOp",EDGE,"E3.1.0.151"),sQuery(id+"F0.wireOp",EDGE,"E3.1.0.152"),sQuery(id+"F0.wireOp",EDGE,"E3.1.0.153"),sQuery(id+"F0.wireOp",EDGE,"E3.1.0.154"),sQuery(id+"F0.wireOp",EDGE,"E3.1.0.155"),sQuery(id+"F0.wireOp",EDGE,"E3.1.0.156"),sQuery(id+"F0.wireOp",EDGE,"E3.1.0.157"),sQuery(id+"F0.wireOp",EDGE,"E3.1.0.158"),sQuery(id+"F0.wireOp",EDGE,"E3.1.0.159"),sQuery(id+"F0.wireOp",EDGE,"E3.1.0.160"),sQuery(id+"F0.wireOp",EDGE,"E3.1.0.161"),sQuery(id+"F0.wireOp",EDGE,"E3.1.0.162"),sQuery(id+"F0.wireOp",EDGE,"E3.1.0.163"),sQuery(id+"F0.wireOp",EDGE,"E3.1.0.164"),sQuery(id+"F0.wireOp",EDGE,"E3.1.0.165"),sQuery(id+"F0.wireOp",EDGE,"E3.1.0.166"),sQuery(id+"F0.wireOp",EDGE,"E3.1.0.167"),sQuery(id+"F0.wireOp",EDGE,"E3.1.0.168"),sQuery(id+"F0.wireOp",EDGE,"E3.1.0.169"),sQuery(id+"F0.wireOp",EDGE,"E4"),sQuery(id+"F0.wireOp",EDGE,"E5"),sQuery(id+"F0.wireOp",EDGE,"E6")])]});
            hole(context, id + "F3", {"style" : HoleStyle.C_BORE, "endStyle" : HoleEndStyle.THROUGH, "standardTappedOrClearance" : lookupTablePath({ "fit" : "Normal", "standard" : "ISO", "size" : "M6", "type" : "Clearance" }), "standardBlindInLast" : lookupTablePath({ "fit" : "Normal", "standard" : "ISO", "engagement" : "75%", "pitch" : "1 mm", "size" : "M6", "type" : "Clearance & tapped" }), "holeDiameter" : 6.6 * mm, "cBoreDiameter" : 11.25 * mm, "cBoreDepth" : 6 * mm, "majorDiameter" : 5 * mm, "isTappedThrough" : true, "tappedDepth" : 12 * mm, "tapClearance" : 3, "locations" : qUnion([Q0, Q1, Q2, Q3, Q4]), "scope" : qUnion([Q5])});
        }
    });
